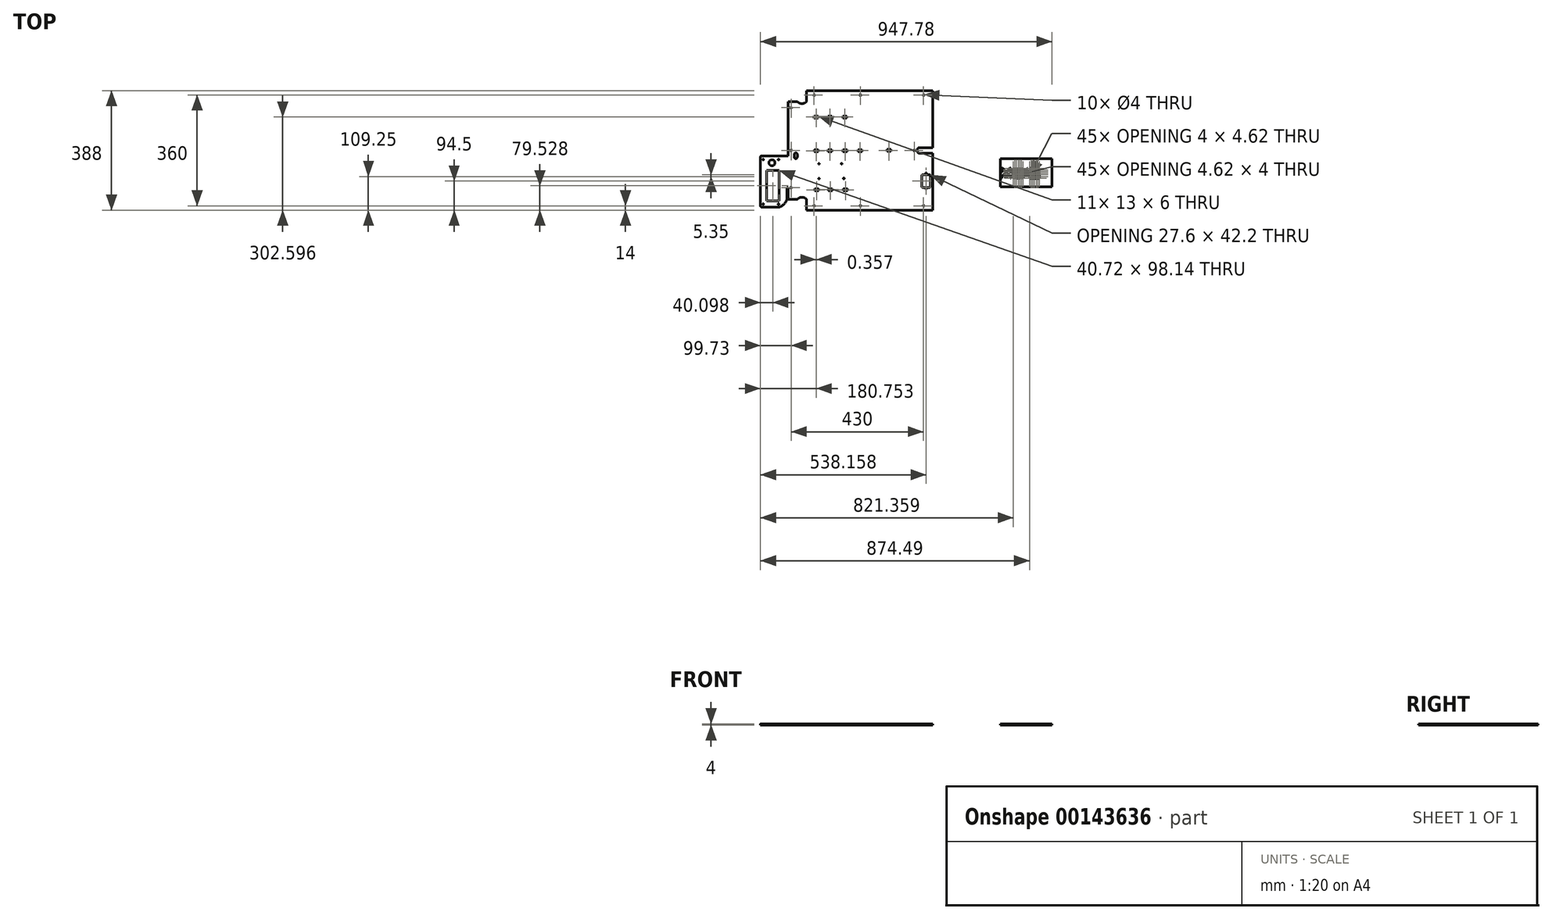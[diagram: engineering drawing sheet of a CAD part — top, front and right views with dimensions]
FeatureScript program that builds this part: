
annotation { "Feature Type Name" : "Feature", "Feature Type Description" : "" }
export const myFeature = defineFeature(function(context is Context, id is Id, definition is map)
    precondition{}
    {
        {
            var Q0;
            Q0=qCreatedBy(makeId("Top.planeOp"),FACE);
            var sketch = newSketch(context, id + "F0", { "sketchPlane" : qUnion([Q0])});
            skLineSegment(sketch, "E0.right", {"start": v(235, 190) * mm, "end": v(235, 20) * mm});
            skPoint(sketch, "E0.middle", {"position": v(0, 0) * mm});
            skLineSegment(sketch, "E1.MirrorCS", {"start": v(215, 190) * mm, "end": v(215, 170) * mm, "construction": true});
            skLineSegment(sketch, "E2.MirrorCS", {"start": v(235, 170) * mm, "end": v(215, 170) * mm, "construction": true});
            skLineSegment(sketch, "E3", {"start": v(215, 170) * mm, "end": v(215, 0) * mm, "construction": true});
            skLineSegment(sketch, "E4", {"start": v(173, 0) * mm, "end": v(215, 0) * mm, "construction": true});
            skLineSegment(sketch, "E5.top", {"start": v(235, 194) * mm, "end": v(-175, 194) * mm});
            skLineSegment(sketch, "E5.left", {"start": v(235, 190) * mm, "end": v(235, 194) * mm});
            skLineSegment(sketch, "E6", {"start": v(-235, 159) * mm, "end": v(-235, 0) * mm});
            skLineSegment(sketch, "E7", {"start": v(-175, 194) * mm, "end": v(-175, 159) * mm});
            skLineSegment(sketch, "E8", {"start": v(-175, 159) * mm, "end": v(-235, 159) * mm});
            skCircle(sketch, "E9", {"center": v(175, 0) * mm, "radius": 2 * mm});
            skCircle(sketch, "E10", {"center": v(-225, 0) * mm, "radius": 2 * mm});
            skLineSegment(sketch, "E11.bottom", {"start": v(199.63, -74) * mm, "end": v(227.23, -74) * mm, "construction": true});
            skLineSegment(sketch, "E11.top", {"start": v(199.63, -125) * mm, "end": v(227.23, -125) * mm, "construction": true});
            skLineSegment(sketch, "E11.left", {"start": v(199.63, -81.4) * mm, "end": v(199.63, -117.6) * mm});
            skLineSegment(sketch, "E11.right", {"start": v(227.23, -81.4) * mm, "end": v(227.23, -117.6) * mm});
            skPoint(sketch, "E11.middle", {"position": v(213.43, -99.5) * mm});
            skCircle(sketch, "E12", {"center": v(213.43, -125) * mm, "radius": 1.5 * mm});
            skCircle(sketch, "E13", {"center": v(213.43, -74) * mm, "radius": 1.5 * mm});
            skLineSegment(sketch, "E14", {"start": v(202.63, -120.6) * mm, "end": v(224.23, -120.6) * mm});
            skLineSegment(sketch, "E15", {"start": v(213.43, -99.5) * mm, "end": v(226.59, -99.5) * mm, "construction": true});
            skLineSegment(sketch, "E16.MirrorCS", {"start": v(202.63, -78.4) * mm, "end": v(224.23, -78.4) * mm});
            skArc(sketch, "E17.filletArc", {"start": v(199.63, -117.6) * mm, "mid": v(200.5, -119.72) * mm, "end": v(202.63, -120.6) * mm});
            skPoint(sketch, "E18.visualSharp", {"position": v(199.63, -78.4) * mm});
            skArc(sketch, "E18.filletArc", {"start": v(202.63, -78.4) * mm, "mid": v(200.5, -79.28) * mm, "end": v(199.63, -81.4) * mm});
            skPoint(sketch, "E19.visualSharp", {"position": v(227.23, -78.4) * mm});
            skArc(sketch, "E19.filletArc", {"start": v(227.23, -81.4) * mm, "mid": v(226.35, -79.28) * mm, "end": v(224.23, -78.4) * mm});
            skArc(sketch, "E20.filletArc", {"start": v(224.23, -120.6) * mm, "mid": v(226.35, -119.72) * mm, "end": v(227.23, -117.6) * mm});
            skLineSegment(sketch, "E21.trimOffspring", {"start": v(-175, 190) * mm, "end": v(235, 190) * mm, "construction": true});
            skPoint(sketch, "E22.orphan", {"position": v(122.36, 0) * mm});
            skCircle(sketch, "E23.MirrorC", {"center": v(-225, 139) * mm, "radius": 2 * mm});
            skLineSegment(sketch, "E24", {"start": v(-235, 0) * mm, "end": v(-210, 0) * mm});
            skPoint(sketch, "E24.endSnap0", {"position": v(-235, -50) * mm});
            skPoint(sketch, "E25", {"position": v(-175, 180) * mm});
            skLineSegment(sketch, "E26", {"start": v(-175, 180) * mm, "end": v(0, 180) * mm, "construction": true});
            skLineSegment(sketch, "E27", {"start": v(0, 180) * mm, "end": v(175, 180) * mm, "construction": true});
            skLineSegment(sketch, "E28", {"start": v(175, 180) * mm, "end": v(235, 180) * mm, "construction": true});
            skCircle(sketch, "E29", {"center": v(-150.66, 180) * mm, "radius": 2 * mm});
            skCircle(sketch, "E30", {"center": v(205, 180) * mm, "radius": 2 * mm});
            skCircle(sketch, "E31", {"center": v(0, 180) * mm, "radius": 2 * mm});
            skLineSegment(sketch, "E32.MirrorCS", {"start": v(-175, -159) * mm, "end": v(-235, -159) * mm});
            skLineSegment(sketch, "E33.MirrorCS", {"start": v(235, -194) * mm, "end": v(-175, -194) * mm});
            skLineSegment(sketch, "E34.MirrorCS", {"start": v(235, -190) * mm, "end": v(235, -20) * mm});
            skLineSegment(sketch, "E35.MirrorCS", {"start": v(235, -190) * mm, "end": v(235, -194) * mm});
            skLineSegment(sketch, "E36.MirrorCS", {"start": v(-175, -194) * mm, "end": v(-175, -159) * mm});
            skCircle(sketch, "E37.MirrorC", {"center": v(-225, -121) * mm, "radius": 2 * mm});
            skCircle(sketch, "E38.MirrorC", {"center": v(-150.66, -180) * mm, "radius": 2 * mm});
            skCircle(sketch, "E39.MirrorC", {"center": v(0, -180) * mm, "radius": 2 * mm});
            skCircle(sketch, "E40.MirrorC", {"center": v(205, -180) * mm, "radius": 2 * mm});
            skLineSegment(sketch, "E41", {"start": v(160.22, 194) * mm, "end": v(160.22, -194) * mm, "construction": true});
            skPoint(sketch, "E42", {"position": v(160.22, 155.68) * mm});
            skLineSegment(sketch, "E43", {"start": v(160.22, 155.68) * mm, "end": v(160.22, 194) * mm});
            skLineSegment(sketch, "E44", {"start": v(-175, 155.68) * mm, "end": v(-175, 159) * mm});
            skLineSegment(sketch, "E45.MirrorCS", {"start": v(-175, -155.68) * mm, "end": v(-175, -159) * mm});
            skLineSegment(sketch, "E46", {"start": v(160.22, -155.68) * mm, "end": v(160.22, -194) * mm});
            skCircle(sketch, "E47", {"center": v(-315.8, -174.64) * mm, "radius": 1.5 * mm});
            skCircle(sketch, "E48", {"center": v(-265.85, -174.82) * mm, "radius": 1.5 * mm});
            skCircle(sketch, "E49", {"center": v(-265.85, -29.64) * mm, "radius": 1.5 * mm});
            skCircle(sketch, "E50", {"center": v(-315.85, -29.64) * mm, "radius": 1.5 * mm});
            skLineSegment(sketch, "E51", {"start": v(-235, -184.73) * mm, "end": v(-319.73, -184.73) * mm});
            skLineSegment(sketch, "E52", {"start": v(-324.73, -179.73) * mm, "end": v(-324.73, -21.83) * mm});
            skPoint(sketch, "E53.visualSharp", {"position": v(-324.73, -184.73) * mm});
            skArc(sketch, "E53.filletArc", {"start": v(-324.73, -179.73) * mm, "mid": v(-323.27, -183.27) * mm, "end": v(-319.73, -184.73) * mm});
            skPoint(sketch, "E54.visualSharp", {"position": v(-324.73, -19.02) * mm});
            skArc(sketch, "E54.filletArc", {"start": v(-322.37, -17.58) * mm, "mid": v(-324.1, -19.4) * mm, "end": v(-324.73, -21.83) * mm});
            skCircle(sketch, "E55", {"center": v(-53.85, -91.06) * mm, "radius": 1.5 * mm});
            skCircle(sketch, "E56", {"center": v(-61.23, -43.24) * mm, "radius": 1.5 * mm});
            skCircle(sketch, "E57", {"center": v(-134.56, -43.33) * mm, "radius": 1.5 * mm});
            skCircle(sketch, "E58", {"center": v(-134.56, -91.36) * mm, "radius": 1.5 * mm});
            skCircle(sketch, "E59.MirrorC", {"center": v(-287.35, -40.12) * mm, "radius": 10 * mm});
            skLineSegment(sketch, "E60.bottom", {"start": v(-305, -163.54) * mm, "end": v(-305, -65.4) * mm});
            skLineSegment(sketch, "E60.top", {"start": v(-264.27, -163.54) * mm, "end": v(-264.27, -65.4) * mm});
            skLineSegment(sketch, "E60.left", {"start": v(-305, -163.54) * mm, "end": v(-264.27, -163.54) * mm});
            skLineSegment(sketch, "E60.right", {"start": v(-305, -65.4) * mm, "end": v(-264.27, -65.4) * mm});
            skLineSegment(sketch, "E61", {"start": v(-322.37, -17.58) * mm, "end": v(-235, -17.58) * mm});
            skLineSegment(sketch, "E62", {"start": v(-235, -141.11) * mm, "end": v(-235, -141) * mm});
            skLineSegment(sketch, "E63", {"start": v(-235, -17.58) * mm, "end": v(-235, 18) * mm});
            skLineSegment(sketch, "E64", {"start": v(-235, -184.73) * mm, "end": v(-235, -119.54) * mm});
            skLineSegment(sketch, "E65", {"start": v(388.05, 194) * mm, "end": v(623.05, 194) * mm});
            skLineSegment(sketch, "E66", {"start": v(623.05, 194) * mm, "end": v(623.05, -194) * mm});
            skPoint(sketch, "E67", {"position": v(488.05, 194) * mm});
            skArc(sketch, "E68", {"start": v(488.05, 194) * mm, "mid": v(391.69, 0) * mm, "end": v(488.05, -194) * mm});
            skLineSegment(sketch, "E69", {"start": v(488.05, -194) * mm, "end": v(623.05, -194) * mm});
            skLineSegment(sketch, "E70.bottom", {"start": v(532.63, -94) * mm, "end": v(492.63, -94) * mm, "construction": true});
            skLineSegment(sketch, "E70.top", {"start": v(532.63, -54) * mm, "end": v(492.63, -54) * mm, "construction": true});
            skLineSegment(sketch, "E70.left", {"start": v(532.63, -94) * mm, "end": v(532.63, -54) * mm, "construction": true});
            skLineSegment(sketch, "E70.right", {"start": v(492.63, -94) * mm, "end": v(492.63, -54) * mm, "construction": true});
            skPoint(sketch, "E70.middle", {"position": v(512.63, -74) * mm});
            skLineSegment(sketch, "E71.bottom", {"start": v(585.76, -94) * mm, "end": v(545.76, -94) * mm, "construction": true});
            skLineSegment(sketch, "E71.top", {"start": v(585.76, -54) * mm, "end": v(545.76, -54) * mm, "construction": true});
            skLineSegment(sketch, "E71.left", {"start": v(585.76, -94) * mm, "end": v(585.76, -54) * mm, "construction": true});
            skLineSegment(sketch, "E71.right", {"start": v(545.76, -94) * mm, "end": v(545.76, -54) * mm, "construction": true});
            skPoint(sketch, "E71.middle", {"position": v(565.76, -74) * mm});
            skLineSegment(sketch, "E72", {"start": v(532.63, -54) * mm, "end": v(545.76, -54) * mm, "construction": true});
            skLineSegment(sketch, "E73.bottom", {"start": v(528.63, -58) * mm, "end": v(496.63, -58) * mm, "construction": true});
            skLineSegment(sketch, "E73.top", {"start": v(528.63, -90) * mm, "end": v(496.63, -90) * mm, "construction": true});
            skLineSegment(sketch, "E73.left", {"start": v(528.63, -58) * mm, "end": v(528.63, -90) * mm, "construction": true});
            skLineSegment(sketch, "E73.right", {"start": v(496.63, -58) * mm, "end": v(496.63, -90) * mm, "construction": true});
            skLineSegment(sketch, "E74.bottom", {"start": v(581.76, -58) * mm, "end": v(549.76, -58) * mm, "construction": true});
            skLineSegment(sketch, "E74.top", {"start": v(581.76, -90) * mm, "end": v(549.76, -90) * mm, "construction": true});
            skLineSegment(sketch, "E74.left", {"start": v(581.76, -58) * mm, "end": v(581.76, -90) * mm, "construction": true});
            skLineSegment(sketch, "E74.right", {"start": v(549.76, -58) * mm, "end": v(549.76, -90) * mm, "construction": true});
            skLineSegment(sketch, "E75.0.1.0", {"start": v(495.47, -61.35) * mm, "end": v(497.78, -61.35) * mm});
            skPoint(sketch, "E75.0.1.1", {"position": v(496.63, -61.35) * mm});
            skLineSegment(sketch, "E75.0.1.2", {"start": v(497.78, -61.35) * mm, "end": v(498.94, -63.35) * mm});
            skLineSegment(sketch, "E75.0.1.3", {"start": v(495.47, -65.35) * mm, "end": v(494.32, -63.35) * mm});
            skLineSegment(sketch, "E75.0.1.4", {"start": v(497.78, -65.35) * mm, "end": v(495.47, -65.35) * mm});
            skCircle(sketch, "E75.0.1.5", {"center": v(496.63, -63.35) * mm, "radius": 2 * mm, "construction": true});
            skLineSegment(sketch, "E75.0.1.6", {"start": v(494.32, -63.35) * mm, "end": v(495.47, -61.35) * mm});
            skLineSegment(sketch, "E75.0.1.7", {"start": v(498.94, -63.35) * mm, "end": v(497.78, -65.35) * mm});
            skLineSegment(sketch, "E75.0.2.0", {"start": v(495.47, -66.7) * mm, "end": v(497.78, -66.7) * mm});
            skPoint(sketch, "E75.0.2.1", {"position": v(496.63, -66.7) * mm});
            skLineSegment(sketch, "E75.0.2.2", {"start": v(497.78, -66.7) * mm, "end": v(498.94, -68.7) * mm});
            skLineSegment(sketch, "E75.0.2.3", {"start": v(495.47, -70.7) * mm, "end": v(494.32, -68.7) * mm});
            skLineSegment(sketch, "E75.0.2.4", {"start": v(497.78, -70.7) * mm, "end": v(495.47, -70.7) * mm});
            skCircle(sketch, "E75.0.2.5", {"center": v(496.63, -68.7) * mm, "radius": 2 * mm, "construction": true});
            skLineSegment(sketch, "E75.0.2.6", {"start": v(494.32, -68.7) * mm, "end": v(495.47, -66.7) * mm});
            skLineSegment(sketch, "E75.0.2.7", {"start": v(498.94, -68.7) * mm, "end": v(497.78, -70.7) * mm});
            skLineSegment(sketch, "E75.0.3.0", {"start": v(495.47, -72.05) * mm, "end": v(497.78, -72.05) * mm});
            skPoint(sketch, "E75.0.3.1", {"position": v(496.63, -72.05) * mm});
            skLineSegment(sketch, "E75.0.3.2", {"start": v(497.78, -72.05) * mm, "end": v(498.94, -74.05) * mm});
            skLineSegment(sketch, "E75.0.3.3", {"start": v(495.47, -76.05) * mm, "end": v(494.32, -74.05) * mm});
            skLineSegment(sketch, "E75.0.3.4", {"start": v(497.78, -76.05) * mm, "end": v(495.47, -76.05) * mm});
            skCircle(sketch, "E75.0.3.5", {"center": v(496.63, -74.05) * mm, "radius": 2 * mm, "construction": true});
            skLineSegment(sketch, "E75.0.3.6", {"start": v(494.32, -74.05) * mm, "end": v(495.47, -72.05) * mm});
            skLineSegment(sketch, "E75.0.3.7", {"start": v(498.94, -74.05) * mm, "end": v(497.78, -76.05) * mm});
            skLineSegment(sketch, "E75.0.4.0", {"start": v(495.47, -77.4) * mm, "end": v(497.78, -77.4) * mm});
            skPoint(sketch, "E75.0.4.1", {"position": v(496.63, -77.4) * mm});
            skLineSegment(sketch, "E75.0.4.2", {"start": v(497.78, -77.4) * mm, "end": v(498.94, -79.4) * mm});
            skLineSegment(sketch, "E75.0.4.3", {"start": v(495.47, -81.4) * mm, "end": v(494.32, -79.4) * mm});
            skLineSegment(sketch, "E75.0.4.4", {"start": v(497.78, -81.4) * mm, "end": v(495.47, -81.4) * mm});
            skCircle(sketch, "E75.0.4.5", {"center": v(496.63, -79.4) * mm, "radius": 2 * mm, "construction": true});
            skLineSegment(sketch, "E75.0.4.6", {"start": v(494.32, -79.4) * mm, "end": v(495.47, -77.4) * mm});
            skLineSegment(sketch, "E75.0.4.7", {"start": v(498.94, -79.4) * mm, "end": v(497.78, -81.4) * mm});
            skLineSegment(sketch, "E75.0.5.0", {"start": v(495.47, -82.75) * mm, "end": v(497.78, -82.75) * mm});
            skPoint(sketch, "E75.0.5.1", {"position": v(496.63, -82.75) * mm});
            skLineSegment(sketch, "E75.0.5.2", {"start": v(497.78, -82.75) * mm, "end": v(498.94, -84.75) * mm});
            skLineSegment(sketch, "E75.0.5.3", {"start": v(495.47, -86.75) * mm, "end": v(494.32, -84.75) * mm});
            skLineSegment(sketch, "E75.0.5.4", {"start": v(497.78, -86.75) * mm, "end": v(495.47, -86.75) * mm});
            skCircle(sketch, "E75.0.5.5", {"center": v(496.63, -84.75) * mm, "radius": 2 * mm, "construction": true});
            skLineSegment(sketch, "E75.0.5.6", {"start": v(494.32, -84.75) * mm, "end": v(495.47, -82.75) * mm});
            skLineSegment(sketch, "E75.0.5.7", {"start": v(498.94, -84.75) * mm, "end": v(497.78, -86.75) * mm});
            skLineSegment(sketch, "E75.1.0.0", {"start": v(500.82, -56) * mm, "end": v(503.13, -56) * mm});
            skPoint(sketch, "E75.1.0.1", {"position": v(501.98, -56) * mm});
            skLineSegment(sketch, "E75.1.0.2", {"start": v(503.13, -56) * mm, "end": v(504.29, -58) * mm});
            skLineSegment(sketch, "E75.1.0.3", {"start": v(500.82, -60) * mm, "end": v(499.67, -58) * mm});
            skLineSegment(sketch, "E75.1.0.4", {"start": v(503.13, -60) * mm, "end": v(500.82, -60) * mm});
            skCircle(sketch, "E75.1.0.5", {"center": v(501.98, -58) * mm, "radius": 2 * mm, "construction": true});
            skLineSegment(sketch, "E75.1.0.6", {"start": v(499.67, -58) * mm, "end": v(500.82, -56) * mm});
            skLineSegment(sketch, "E75.1.0.7", {"start": v(504.29, -58) * mm, "end": v(503.13, -60) * mm});
            skLineSegment(sketch, "E75.1.1.0", {"start": v(500.82, -61.35) * mm, "end": v(503.13, -61.35) * mm});
            skPoint(sketch, "E75.1.1.1", {"position": v(501.98, -61.35) * mm});
            skLineSegment(sketch, "E75.1.1.2", {"start": v(503.13, -61.35) * mm, "end": v(504.29, -63.35) * mm});
            skLineSegment(sketch, "E75.1.1.3", {"start": v(500.82, -65.35) * mm, "end": v(499.67, -63.35) * mm});
            skLineSegment(sketch, "E75.1.1.4", {"start": v(503.13, -65.35) * mm, "end": v(500.82, -65.35) * mm});
            skCircle(sketch, "E75.1.1.5", {"center": v(501.98, -63.35) * mm, "radius": 2 * mm, "construction": true});
            skLineSegment(sketch, "E75.1.1.6", {"start": v(499.67, -63.35) * mm, "end": v(500.82, -61.35) * mm});
            skLineSegment(sketch, "E75.1.1.7", {"start": v(504.29, -63.35) * mm, "end": v(503.13, -65.35) * mm});
            skLineSegment(sketch, "E75.1.2.0", {"start": v(500.82, -66.7) * mm, "end": v(503.13, -66.7) * mm});
            skPoint(sketch, "E75.1.2.1", {"position": v(501.98, -66.7) * mm});
            skLineSegment(sketch, "E75.1.2.2", {"start": v(503.13, -66.7) * mm, "end": v(504.29, -68.7) * mm});
            skLineSegment(sketch, "E75.1.2.3", {"start": v(500.82, -70.7) * mm, "end": v(499.67, -68.7) * mm});
            skLineSegment(sketch, "E75.1.2.4", {"start": v(503.13, -70.7) * mm, "end": v(500.82, -70.7) * mm});
            skCircle(sketch, "E75.1.2.5", {"center": v(501.98, -68.7) * mm, "radius": 2 * mm, "construction": true});
            skLineSegment(sketch, "E75.1.2.6", {"start": v(499.67, -68.7) * mm, "end": v(500.82, -66.7) * mm});
            skLineSegment(sketch, "E75.1.2.7", {"start": v(504.29, -68.7) * mm, "end": v(503.13, -70.7) * mm});
            skLineSegment(sketch, "E75.1.3.0", {"start": v(500.82, -72.05) * mm, "end": v(503.13, -72.05) * mm});
            skPoint(sketch, "E75.1.3.1", {"position": v(501.98, -72.05) * mm});
            skLineSegment(sketch, "E75.1.3.2", {"start": v(503.13, -72.05) * mm, "end": v(504.29, -74.05) * mm});
            skLineSegment(sketch, "E75.1.3.3", {"start": v(500.82, -76.05) * mm, "end": v(499.67, -74.05) * mm});
            skLineSegment(sketch, "E75.1.3.4", {"start": v(503.13, -76.05) * mm, "end": v(500.82, -76.05) * mm});
            skCircle(sketch, "E75.1.3.5", {"center": v(501.98, -74.05) * mm, "radius": 2 * mm, "construction": true});
            skLineSegment(sketch, "E75.1.3.6", {"start": v(499.67, -74.05) * mm, "end": v(500.82, -72.05) * mm});
            skLineSegment(sketch, "E75.1.3.7", {"start": v(504.29, -74.05) * mm, "end": v(503.13, -76.05) * mm});
            skLineSegment(sketch, "E75.1.4.0", {"start": v(500.82, -77.4) * mm, "end": v(503.13, -77.4) * mm});
            skPoint(sketch, "E75.1.4.1", {"position": v(501.98, -77.4) * mm});
            skLineSegment(sketch, "E75.1.4.2", {"start": v(503.13, -77.4) * mm, "end": v(504.29, -79.4) * mm});
            skLineSegment(sketch, "E75.1.4.3", {"start": v(500.82, -81.4) * mm, "end": v(499.67, -79.4) * mm});
            skLineSegment(sketch, "E75.1.4.4", {"start": v(503.13, -81.4) * mm, "end": v(500.82, -81.4) * mm});
            skCircle(sketch, "E75.1.4.5", {"center": v(501.98, -79.4) * mm, "radius": 2 * mm, "construction": true});
            skLineSegment(sketch, "E75.1.4.6", {"start": v(499.67, -79.4) * mm, "end": v(500.82, -77.4) * mm});
            skLineSegment(sketch, "E75.1.4.7", {"start": v(504.29, -79.4) * mm, "end": v(503.13, -81.4) * mm});
            skLineSegment(sketch, "E75.1.5.0", {"start": v(500.82, -82.75) * mm, "end": v(503.13, -82.75) * mm});
            skPoint(sketch, "E75.1.5.1", {"position": v(501.98, -82.75) * mm});
            skLineSegment(sketch, "E75.1.5.2", {"start": v(503.13, -82.75) * mm, "end": v(504.29, -84.75) * mm});
            skLineSegment(sketch, "E75.1.5.3", {"start": v(500.82, -86.75) * mm, "end": v(499.67, -84.75) * mm});
            skLineSegment(sketch, "E75.1.5.4", {"start": v(503.13, -86.75) * mm, "end": v(500.82, -86.75) * mm});
            skCircle(sketch, "E75.1.5.5", {"center": v(501.98, -84.75) * mm, "radius": 2 * mm, "construction": true});
            skLineSegment(sketch, "E75.1.5.6", {"start": v(499.67, -84.75) * mm, "end": v(500.82, -82.75) * mm});
            skLineSegment(sketch, "E75.1.5.7", {"start": v(504.29, -84.75) * mm, "end": v(503.13, -86.75) * mm});
            skLineSegment(sketch, "E75.1.6.0", {"start": v(500.82, -88.1) * mm, "end": v(503.13, -88.1) * mm});
            skPoint(sketch, "E75.1.6.1", {"position": v(501.98, -88.1) * mm});
            skLineSegment(sketch, "E75.1.6.2", {"start": v(503.13, -88.1) * mm, "end": v(504.29, -90.1) * mm});
            skLineSegment(sketch, "E75.1.6.3", {"start": v(500.82, -92.1) * mm, "end": v(499.67, -90.1) * mm});
            skLineSegment(sketch, "E75.1.6.4", {"start": v(503.13, -92.1) * mm, "end": v(500.82, -92.1) * mm});
            skCircle(sketch, "E75.1.6.5", {"center": v(501.98, -90.1) * mm, "radius": 2 * mm, "construction": true});
            skLineSegment(sketch, "E75.1.6.6", {"start": v(499.67, -90.1) * mm, "end": v(500.82, -88.1) * mm});
            skLineSegment(sketch, "E75.1.6.7", {"start": v(504.29, -90.1) * mm, "end": v(503.13, -92.1) * mm});
            skLineSegment(sketch, "E75.2.0.0", {"start": v(506.17, -56) * mm, "end": v(508.48, -56) * mm});
            skPoint(sketch, "E75.2.0.1", {"position": v(507.33, -56) * mm});
            skLineSegment(sketch, "E75.2.0.2", {"start": v(508.48, -56) * mm, "end": v(509.64, -58) * mm});
            skLineSegment(sketch, "E75.2.0.3", {"start": v(506.17, -60) * mm, "end": v(505.02, -58) * mm});
            skLineSegment(sketch, "E75.2.0.4", {"start": v(508.48, -60) * mm, "end": v(506.17, -60) * mm});
            skCircle(sketch, "E75.2.0.5", {"center": v(507.33, -58) * mm, "radius": 2 * mm, "construction": true});
            skLineSegment(sketch, "E75.2.0.6", {"start": v(505.02, -58) * mm, "end": v(506.17, -56) * mm});
            skLineSegment(sketch, "E75.2.0.7", {"start": v(509.64, -58) * mm, "end": v(508.48, -60) * mm});
            skLineSegment(sketch, "E75.2.1.0", {"start": v(506.17, -61.35) * mm, "end": v(508.48, -61.35) * mm});
            skPoint(sketch, "E75.2.1.1", {"position": v(507.33, -61.35) * mm});
            skLineSegment(sketch, "E75.2.1.2", {"start": v(508.48, -61.35) * mm, "end": v(509.64, -63.35) * mm});
            skLineSegment(sketch, "E75.2.1.3", {"start": v(506.17, -65.35) * mm, "end": v(505.02, -63.35) * mm});
            skLineSegment(sketch, "E75.2.1.4", {"start": v(508.48, -65.35) * mm, "end": v(506.17, -65.35) * mm});
            skCircle(sketch, "E75.2.1.5", {"center": v(507.33, -63.35) * mm, "radius": 2 * mm, "construction": true});
            skLineSegment(sketch, "E75.2.1.6", {"start": v(505.02, -63.35) * mm, "end": v(506.17, -61.35) * mm});
            skLineSegment(sketch, "E75.2.1.7", {"start": v(509.64, -63.35) * mm, "end": v(508.48, -65.35) * mm});
            skLineSegment(sketch, "E75.2.2.0", {"start": v(506.17, -66.7) * mm, "end": v(508.48, -66.7) * mm});
            skPoint(sketch, "E75.2.2.1", {"position": v(507.33, -66.7) * mm});
            skLineSegment(sketch, "E75.2.2.2", {"start": v(508.48, -66.7) * mm, "end": v(509.64, -68.7) * mm});
            skLineSegment(sketch, "E75.2.2.3", {"start": v(506.17, -70.7) * mm, "end": v(505.02, -68.7) * mm});
            skLineSegment(sketch, "E75.2.2.4", {"start": v(508.48, -70.7) * mm, "end": v(506.17, -70.7) * mm});
            skCircle(sketch, "E75.2.2.5", {"center": v(507.33, -68.7) * mm, "radius": 2 * mm, "construction": true});
            skLineSegment(sketch, "E75.2.2.6", {"start": v(505.02, -68.7) * mm, "end": v(506.17, -66.7) * mm});
            skLineSegment(sketch, "E75.2.2.7", {"start": v(509.64, -68.7) * mm, "end": v(508.48, -70.7) * mm});
            skLineSegment(sketch, "E75.2.3.0", {"start": v(506.17, -72.05) * mm, "end": v(508.48, -72.05) * mm});
            skPoint(sketch, "E75.2.3.1", {"position": v(507.33, -72.05) * mm});
            skLineSegment(sketch, "E75.2.3.2", {"start": v(508.48, -72.05) * mm, "end": v(509.64, -74.05) * mm});
            skLineSegment(sketch, "E75.2.3.3", {"start": v(506.17, -76.05) * mm, "end": v(505.02, -74.05) * mm});
            skLineSegment(sketch, "E75.2.3.4", {"start": v(508.48, -76.05) * mm, "end": v(506.17, -76.05) * mm});
            skCircle(sketch, "E75.2.3.5", {"center": v(507.33, -74.05) * mm, "radius": 2 * mm, "construction": true});
            skLineSegment(sketch, "E75.2.3.6", {"start": v(505.02, -74.05) * mm, "end": v(506.17, -72.05) * mm});
            skLineSegment(sketch, "E75.2.3.7", {"start": v(509.64, -74.05) * mm, "end": v(508.48, -76.05) * mm});
            skLineSegment(sketch, "E75.2.4.0", {"start": v(506.17, -77.4) * mm, "end": v(508.48, -77.4) * mm});
            skPoint(sketch, "E75.2.4.1", {"position": v(507.33, -77.4) * mm});
            skLineSegment(sketch, "E75.2.4.2", {"start": v(508.48, -77.4) * mm, "end": v(509.64, -79.4) * mm});
            skLineSegment(sketch, "E75.2.4.3", {"start": v(506.17, -81.4) * mm, "end": v(505.02, -79.4) * mm});
            skLineSegment(sketch, "E75.2.4.4", {"start": v(508.48, -81.4) * mm, "end": v(506.17, -81.4) * mm});
            skCircle(sketch, "E75.2.4.5", {"center": v(507.33, -79.4) * mm, "radius": 2 * mm, "construction": true});
            skLineSegment(sketch, "E75.2.4.6", {"start": v(505.02, -79.4) * mm, "end": v(506.17, -77.4) * mm});
            skLineSegment(sketch, "E75.2.4.7", {"start": v(509.64, -79.4) * mm, "end": v(508.48, -81.4) * mm});
            skLineSegment(sketch, "E75.2.5.0", {"start": v(506.17, -82.75) * mm, "end": v(508.48, -82.75) * mm});
            skPoint(sketch, "E75.2.5.1", {"position": v(507.33, -82.75) * mm});
            skLineSegment(sketch, "E75.2.5.2", {"start": v(508.48, -82.75) * mm, "end": v(509.64, -84.75) * mm});
            skLineSegment(sketch, "E75.2.5.3", {"start": v(506.17, -86.75) * mm, "end": v(505.02, -84.75) * mm});
            skLineSegment(sketch, "E75.2.5.4", {"start": v(508.48, -86.75) * mm, "end": v(506.17, -86.75) * mm});
            skCircle(sketch, "E75.2.5.5", {"center": v(507.33, -84.75) * mm, "radius": 2 * mm, "construction": true});
            skLineSegment(sketch, "E75.2.5.6", {"start": v(505.02, -84.75) * mm, "end": v(506.17, -82.75) * mm});
            skLineSegment(sketch, "E75.2.5.7", {"start": v(509.64, -84.75) * mm, "end": v(508.48, -86.75) * mm});
            skLineSegment(sketch, "E75.2.6.0", {"start": v(506.17, -88.1) * mm, "end": v(508.48, -88.1) * mm});
            skPoint(sketch, "E75.2.6.1", {"position": v(507.33, -88.1) * mm});
            skLineSegment(sketch, "E75.2.6.2", {"start": v(508.48, -88.1) * mm, "end": v(509.64, -90.1) * mm});
            skLineSegment(sketch, "E75.2.6.3", {"start": v(506.17, -92.1) * mm, "end": v(505.02, -90.1) * mm});
            skLineSegment(sketch, "E75.2.6.4", {"start": v(508.48, -92.1) * mm, "end": v(506.17, -92.1) * mm});
            skCircle(sketch, "E75.2.6.5", {"center": v(507.33, -90.1) * mm, "radius": 2 * mm, "construction": true});
            skLineSegment(sketch, "E75.2.6.6", {"start": v(505.02, -90.1) * mm, "end": v(506.17, -88.1) * mm});
            skLineSegment(sketch, "E75.2.6.7", {"start": v(509.64, -90.1) * mm, "end": v(508.48, -92.1) * mm});
            skLineSegment(sketch, "E75.3.0.0", {"start": v(511.52, -56) * mm, "end": v(513.83, -56) * mm});
            skPoint(sketch, "E75.3.0.1", {"position": v(512.68, -56) * mm});
            skLineSegment(sketch, "E75.3.0.2", {"start": v(513.83, -56) * mm, "end": v(514.99, -58) * mm});
            skLineSegment(sketch, "E75.3.0.3", {"start": v(511.52, -60) * mm, "end": v(510.37, -58) * mm});
            skLineSegment(sketch, "E75.3.0.4", {"start": v(513.83, -60) * mm, "end": v(511.52, -60) * mm});
            skCircle(sketch, "E75.3.0.5", {"center": v(512.68, -58) * mm, "radius": 2 * mm, "construction": true});
            skLineSegment(sketch, "E75.3.0.6", {"start": v(510.37, -58) * mm, "end": v(511.52, -56) * mm});
            skLineSegment(sketch, "E75.3.0.7", {"start": v(514.99, -58) * mm, "end": v(513.83, -60) * mm});
            skLineSegment(sketch, "E75.3.1.0", {"start": v(511.52, -61.35) * mm, "end": v(513.83, -61.35) * mm});
            skPoint(sketch, "E75.3.1.1", {"position": v(512.68, -61.35) * mm});
            skLineSegment(sketch, "E75.3.1.2", {"start": v(513.83, -61.35) * mm, "end": v(514.99, -63.35) * mm});
            skLineSegment(sketch, "E75.3.1.3", {"start": v(511.52, -65.35) * mm, "end": v(510.37, -63.35) * mm});
            skLineSegment(sketch, "E75.3.1.4", {"start": v(513.83, -65.35) * mm, "end": v(511.52, -65.35) * mm});
            skCircle(sketch, "E75.3.1.5", {"center": v(512.68, -63.35) * mm, "radius": 2 * mm, "construction": true});
            skLineSegment(sketch, "E75.3.1.6", {"start": v(510.37, -63.35) * mm, "end": v(511.52, -61.35) * mm});
            skLineSegment(sketch, "E75.3.1.7", {"start": v(514.99, -63.35) * mm, "end": v(513.83, -65.35) * mm});
            skLineSegment(sketch, "E75.3.2.0", {"start": v(511.52, -66.7) * mm, "end": v(513.83, -66.7) * mm});
            skPoint(sketch, "E75.3.2.1", {"position": v(512.68, -66.7) * mm});
            skLineSegment(sketch, "E75.3.2.2", {"start": v(513.83, -66.7) * mm, "end": v(514.99, -68.7) * mm});
            skLineSegment(sketch, "E75.3.2.3", {"start": v(511.52, -70.7) * mm, "end": v(510.37, -68.7) * mm});
            skLineSegment(sketch, "E75.3.2.4", {"start": v(513.83, -70.7) * mm, "end": v(511.52, -70.7) * mm});
            skCircle(sketch, "E75.3.2.5", {"center": v(512.68, -68.7) * mm, "radius": 2 * mm, "construction": true});
            skLineSegment(sketch, "E75.3.2.6", {"start": v(510.37, -68.7) * mm, "end": v(511.52, -66.7) * mm});
            skLineSegment(sketch, "E75.3.2.7", {"start": v(514.99, -68.7) * mm, "end": v(513.83, -70.7) * mm});
            skLineSegment(sketch, "E75.3.3.0", {"start": v(511.52, -72.05) * mm, "end": v(513.83, -72.05) * mm});
            skPoint(sketch, "E75.3.3.1", {"position": v(512.68, -72.05) * mm});
            skLineSegment(sketch, "E75.3.3.2", {"start": v(513.83, -72.05) * mm, "end": v(514.99, -74.05) * mm});
            skLineSegment(sketch, "E75.3.3.3", {"start": v(511.52, -76.05) * mm, "end": v(510.37, -74.05) * mm});
            skLineSegment(sketch, "E75.3.3.4", {"start": v(513.83, -76.05) * mm, "end": v(511.52, -76.05) * mm});
            skCircle(sketch, "E75.3.3.5", {"center": v(512.68, -74.05) * mm, "radius": 2 * mm, "construction": true});
            skLineSegment(sketch, "E75.3.3.6", {"start": v(510.37, -74.05) * mm, "end": v(511.52, -72.05) * mm});
            skLineSegment(sketch, "E75.3.3.7", {"start": v(514.99, -74.05) * mm, "end": v(513.83, -76.05) * mm});
            skLineSegment(sketch, "E75.3.4.0", {"start": v(511.52, -77.4) * mm, "end": v(513.83, -77.4) * mm});
            skPoint(sketch, "E75.3.4.1", {"position": v(512.68, -77.4) * mm});
            skLineSegment(sketch, "E75.3.4.2", {"start": v(513.83, -77.4) * mm, "end": v(514.99, -79.4) * mm});
            skLineSegment(sketch, "E75.3.4.3", {"start": v(511.52, -81.4) * mm, "end": v(510.37, -79.4) * mm});
            skLineSegment(sketch, "E75.3.4.4", {"start": v(513.83, -81.4) * mm, "end": v(511.52, -81.4) * mm});
            skCircle(sketch, "E75.3.4.5", {"center": v(512.68, -79.4) * mm, "radius": 2 * mm, "construction": true});
            skLineSegment(sketch, "E75.3.4.6", {"start": v(510.37, -79.4) * mm, "end": v(511.52, -77.4) * mm});
            skLineSegment(sketch, "E75.3.4.7", {"start": v(514.99, -79.4) * mm, "end": v(513.83, -81.4) * mm});
            skLineSegment(sketch, "E75.3.5.0", {"start": v(511.52, -82.75) * mm, "end": v(513.83, -82.75) * mm});
            skPoint(sketch, "E75.3.5.1", {"position": v(512.68, -82.75) * mm});
            skLineSegment(sketch, "E75.3.5.2", {"start": v(513.83, -82.75) * mm, "end": v(514.99, -84.75) * mm});
            skLineSegment(sketch, "E75.3.5.3", {"start": v(511.52, -86.75) * mm, "end": v(510.37, -84.75) * mm});
            skLineSegment(sketch, "E75.3.5.4", {"start": v(513.83, -86.75) * mm, "end": v(511.52, -86.75) * mm});
            skCircle(sketch, "E75.3.5.5", {"center": v(512.68, -84.75) * mm, "radius": 2 * mm, "construction": true});
            skLineSegment(sketch, "E75.3.5.6", {"start": v(510.37, -84.75) * mm, "end": v(511.52, -82.75) * mm});
            skLineSegment(sketch, "E75.3.5.7", {"start": v(514.99, -84.75) * mm, "end": v(513.83, -86.75) * mm});
            skLineSegment(sketch, "E75.3.6.0", {"start": v(511.52, -88.1) * mm, "end": v(513.83, -88.1) * mm});
            skPoint(sketch, "E75.3.6.1", {"position": v(512.68, -88.1) * mm});
            skLineSegment(sketch, "E75.3.6.2", {"start": v(513.83, -88.1) * mm, "end": v(514.99, -90.1) * mm});
            skLineSegment(sketch, "E75.3.6.3", {"start": v(511.52, -92.1) * mm, "end": v(510.37, -90.1) * mm});
            skLineSegment(sketch, "E75.3.6.4", {"start": v(513.83, -92.1) * mm, "end": v(511.52, -92.1) * mm});
            skCircle(sketch, "E75.3.6.5", {"center": v(512.68, -90.1) * mm, "radius": 2 * mm, "construction": true});
            skLineSegment(sketch, "E75.3.6.6", {"start": v(510.37, -90.1) * mm, "end": v(511.52, -88.1) * mm});
            skLineSegment(sketch, "E75.3.6.7", {"start": v(514.99, -90.1) * mm, "end": v(513.83, -92.1) * mm});
            skLineSegment(sketch, "E75.4.0.0", {"start": v(516.87, -56) * mm, "end": v(519.18, -56) * mm});
            skPoint(sketch, "E75.4.0.1", {"position": v(518.03, -56) * mm});
            skLineSegment(sketch, "E75.4.0.2", {"start": v(519.18, -56) * mm, "end": v(520.34, -58) * mm});
            skLineSegment(sketch, "E75.4.0.3", {"start": v(516.87, -60) * mm, "end": v(515.72, -58) * mm});
            skLineSegment(sketch, "E75.4.0.4", {"start": v(519.18, -60) * mm, "end": v(516.87, -60) * mm});
            skCircle(sketch, "E75.4.0.5", {"center": v(518.03, -58) * mm, "radius": 2 * mm, "construction": true});
            skLineSegment(sketch, "E75.4.0.6", {"start": v(515.72, -58) * mm, "end": v(516.87, -56) * mm});
            skLineSegment(sketch, "E75.4.0.7", {"start": v(520.34, -58) * mm, "end": v(519.18, -60) * mm});
            skLineSegment(sketch, "E75.4.1.0", {"start": v(516.87, -61.35) * mm, "end": v(519.18, -61.35) * mm});
            skPoint(sketch, "E75.4.1.1", {"position": v(518.03, -61.35) * mm});
            skLineSegment(sketch, "E75.4.1.2", {"start": v(519.18, -61.35) * mm, "end": v(520.34, -63.35) * mm});
            skLineSegment(sketch, "E75.4.1.3", {"start": v(516.87, -65.35) * mm, "end": v(515.72, -63.35) * mm});
            skLineSegment(sketch, "E75.4.1.4", {"start": v(519.18, -65.35) * mm, "end": v(516.87, -65.35) * mm});
            skCircle(sketch, "E75.4.1.5", {"center": v(518.03, -63.35) * mm, "radius": 2 * mm, "construction": true});
            skLineSegment(sketch, "E75.4.1.6", {"start": v(515.72, -63.35) * mm, "end": v(516.87, -61.35) * mm});
            skLineSegment(sketch, "E75.4.1.7", {"start": v(520.34, -63.35) * mm, "end": v(519.18, -65.35) * mm});
            skLineSegment(sketch, "E75.4.2.0", {"start": v(516.87, -66.7) * mm, "end": v(519.18, -66.7) * mm});
            skPoint(sketch, "E75.4.2.1", {"position": v(518.03, -66.7) * mm});
            skLineSegment(sketch, "E75.4.2.2", {"start": v(519.18, -66.7) * mm, "end": v(520.34, -68.7) * mm});
            skLineSegment(sketch, "E75.4.2.3", {"start": v(516.87, -70.7) * mm, "end": v(515.72, -68.7) * mm});
            skLineSegment(sketch, "E75.4.2.4", {"start": v(519.18, -70.7) * mm, "end": v(516.87, -70.7) * mm});
            skCircle(sketch, "E75.4.2.5", {"center": v(518.03, -68.7) * mm, "radius": 2 * mm, "construction": true});
            skLineSegment(sketch, "E75.4.2.6", {"start": v(515.72, -68.7) * mm, "end": v(516.87, -66.7) * mm});
            skLineSegment(sketch, "E75.4.2.7", {"start": v(520.34, -68.7) * mm, "end": v(519.18, -70.7) * mm});
            skLineSegment(sketch, "E75.4.3.0", {"start": v(516.87, -72.05) * mm, "end": v(519.18, -72.05) * mm});
            skPoint(sketch, "E75.4.3.1", {"position": v(518.03, -72.05) * mm});
            skLineSegment(sketch, "E75.4.3.2", {"start": v(519.18, -72.05) * mm, "end": v(520.34, -74.05) * mm});
            skLineSegment(sketch, "E75.4.3.3", {"start": v(516.87, -76.05) * mm, "end": v(515.72, -74.05) * mm});
            skLineSegment(sketch, "E75.4.3.4", {"start": v(519.18, -76.05) * mm, "end": v(516.87, -76.05) * mm});
            skCircle(sketch, "E75.4.3.5", {"center": v(518.03, -74.05) * mm, "radius": 2 * mm, "construction": true});
            skLineSegment(sketch, "E75.4.3.6", {"start": v(515.72, -74.05) * mm, "end": v(516.87, -72.05) * mm});
            skLineSegment(sketch, "E75.4.3.7", {"start": v(520.34, -74.05) * mm, "end": v(519.18, -76.05) * mm});
            skLineSegment(sketch, "E75.4.4.0", {"start": v(516.87, -77.4) * mm, "end": v(519.18, -77.4) * mm});
            skPoint(sketch, "E75.4.4.1", {"position": v(518.03, -77.4) * mm});
            skLineSegment(sketch, "E75.4.4.2", {"start": v(519.18, -77.4) * mm, "end": v(520.34, -79.4) * mm});
            skLineSegment(sketch, "E75.4.4.3", {"start": v(516.87, -81.4) * mm, "end": v(515.72, -79.4) * mm});
            skLineSegment(sketch, "E75.4.4.4", {"start": v(519.18, -81.4) * mm, "end": v(516.87, -81.4) * mm});
            skCircle(sketch, "E75.4.4.5", {"center": v(518.03, -79.4) * mm, "radius": 2 * mm, "construction": true});
            skLineSegment(sketch, "E75.4.4.6", {"start": v(515.72, -79.4) * mm, "end": v(516.87, -77.4) * mm});
            skLineSegment(sketch, "E75.4.4.7", {"start": v(520.34, -79.4) * mm, "end": v(519.18, -81.4) * mm});
            skLineSegment(sketch, "E75.4.5.0", {"start": v(516.87, -82.75) * mm, "end": v(519.18, -82.75) * mm});
            skPoint(sketch, "E75.4.5.1", {"position": v(518.03, -82.75) * mm});
            skLineSegment(sketch, "E75.4.5.2", {"start": v(519.18, -82.75) * mm, "end": v(520.34, -84.75) * mm});
            skLineSegment(sketch, "E75.4.5.3", {"start": v(516.87, -86.75) * mm, "end": v(515.72, -84.75) * mm});
            skLineSegment(sketch, "E75.4.5.4", {"start": v(519.18, -86.75) * mm, "end": v(516.87, -86.75) * mm});
            skCircle(sketch, "E75.4.5.5", {"center": v(518.03, -84.75) * mm, "radius": 2 * mm, "construction": true});
            skLineSegment(sketch, "E75.4.5.6", {"start": v(515.72, -84.75) * mm, "end": v(516.87, -82.75) * mm});
            skLineSegment(sketch, "E75.4.5.7", {"start": v(520.34, -84.75) * mm, "end": v(519.18, -86.75) * mm});
            skLineSegment(sketch, "E75.4.6.0", {"start": v(516.87, -88.1) * mm, "end": v(519.18, -88.1) * mm});
            skPoint(sketch, "E75.4.6.1", {"position": v(518.03, -88.1) * mm});
            skLineSegment(sketch, "E75.4.6.2", {"start": v(519.18, -88.1) * mm, "end": v(520.34, -90.1) * mm});
            skLineSegment(sketch, "E75.4.6.3", {"start": v(516.87, -92.1) * mm, "end": v(515.72, -90.1) * mm});
            skLineSegment(sketch, "E75.4.6.4", {"start": v(519.18, -92.1) * mm, "end": v(516.87, -92.1) * mm});
            skCircle(sketch, "E75.4.6.5", {"center": v(518.03, -90.1) * mm, "radius": 2 * mm, "construction": true});
            skLineSegment(sketch, "E75.4.6.6", {"start": v(515.72, -90.1) * mm, "end": v(516.87, -88.1) * mm});
            skLineSegment(sketch, "E75.4.6.7", {"start": v(520.34, -90.1) * mm, "end": v(519.18, -92.1) * mm});
            skLineSegment(sketch, "E75.5.0.0", {"start": v(522.22, -56) * mm, "end": v(524.53, -56) * mm});
            skPoint(sketch, "E75.5.0.1", {"position": v(523.38, -56) * mm});
            skLineSegment(sketch, "E75.5.0.2", {"start": v(524.53, -56) * mm, "end": v(525.69, -58) * mm});
            skLineSegment(sketch, "E75.5.0.3", {"start": v(522.22, -60) * mm, "end": v(521.07, -58) * mm});
            skLineSegment(sketch, "E75.5.0.4", {"start": v(524.53, -60) * mm, "end": v(522.22, -60) * mm});
            skCircle(sketch, "E75.5.0.5", {"center": v(523.38, -58) * mm, "radius": 2 * mm, "construction": true});
            skLineSegment(sketch, "E75.5.0.6", {"start": v(521.07, -58) * mm, "end": v(522.22, -56) * mm});
            skLineSegment(sketch, "E75.5.0.7", {"start": v(525.69, -58) * mm, "end": v(524.53, -60) * mm});
            skLineSegment(sketch, "E75.5.1.0", {"start": v(522.22, -61.35) * mm, "end": v(524.53, -61.35) * mm});
            skPoint(sketch, "E75.5.1.1", {"position": v(523.38, -61.35) * mm});
            skLineSegment(sketch, "E75.5.1.2", {"start": v(524.53, -61.35) * mm, "end": v(525.69, -63.35) * mm});
            skLineSegment(sketch, "E75.5.1.3", {"start": v(522.22, -65.35) * mm, "end": v(521.07, -63.35) * mm});
            skLineSegment(sketch, "E75.5.1.4", {"start": v(524.53, -65.35) * mm, "end": v(522.22, -65.35) * mm});
            skCircle(sketch, "E75.5.1.5", {"center": v(523.38, -63.35) * mm, "radius": 2 * mm, "construction": true});
            skLineSegment(sketch, "E75.5.1.6", {"start": v(521.07, -63.35) * mm, "end": v(522.22, -61.35) * mm});
            skLineSegment(sketch, "E75.5.1.7", {"start": v(525.69, -63.35) * mm, "end": v(524.53, -65.35) * mm});
            skLineSegment(sketch, "E75.5.2.0", {"start": v(522.22, -66.7) * mm, "end": v(524.53, -66.7) * mm});
            skPoint(sketch, "E75.5.2.1", {"position": v(523.38, -66.7) * mm});
            skLineSegment(sketch, "E75.5.2.2", {"start": v(524.53, -66.7) * mm, "end": v(525.69, -68.7) * mm});
            skLineSegment(sketch, "E75.5.2.3", {"start": v(522.22, -70.7) * mm, "end": v(521.07, -68.7) * mm});
            skLineSegment(sketch, "E75.5.2.4", {"start": v(524.53, -70.7) * mm, "end": v(522.22, -70.7) * mm});
            skCircle(sketch, "E75.5.2.5", {"center": v(523.38, -68.7) * mm, "radius": 2 * mm, "construction": true});
            skLineSegment(sketch, "E75.5.2.6", {"start": v(521.07, -68.7) * mm, "end": v(522.22, -66.7) * mm});
            skLineSegment(sketch, "E75.5.2.7", {"start": v(525.69, -68.7) * mm, "end": v(524.53, -70.7) * mm});
            skLineSegment(sketch, "E75.5.3.0", {"start": v(522.22, -72.05) * mm, "end": v(524.53, -72.05) * mm});
            skPoint(sketch, "E75.5.3.1", {"position": v(523.38, -72.05) * mm});
            skLineSegment(sketch, "E75.5.3.2", {"start": v(524.53, -72.05) * mm, "end": v(525.69, -74.05) * mm});
            skLineSegment(sketch, "E75.5.3.3", {"start": v(522.22, -76.05) * mm, "end": v(521.07, -74.05) * mm});
            skLineSegment(sketch, "E75.5.3.4", {"start": v(524.53, -76.05) * mm, "end": v(522.22, -76.05) * mm});
            skCircle(sketch, "E75.5.3.5", {"center": v(523.38, -74.05) * mm, "radius": 2 * mm, "construction": true});
            skLineSegment(sketch, "E75.5.3.6", {"start": v(521.07, -74.05) * mm, "end": v(522.22, -72.05) * mm});
            skLineSegment(sketch, "E75.5.3.7", {"start": v(525.69, -74.05) * mm, "end": v(524.53, -76.05) * mm});
            skLineSegment(sketch, "E75.5.4.0", {"start": v(522.22, -77.4) * mm, "end": v(524.53, -77.4) * mm});
            skPoint(sketch, "E75.5.4.1", {"position": v(523.38, -77.4) * mm});
            skLineSegment(sketch, "E75.5.4.2", {"start": v(524.53, -77.4) * mm, "end": v(525.69, -79.4) * mm});
            skLineSegment(sketch, "E75.5.4.3", {"start": v(522.22, -81.4) * mm, "end": v(521.07, -79.4) * mm});
            skLineSegment(sketch, "E75.5.4.4", {"start": v(524.53, -81.4) * mm, "end": v(522.22, -81.4) * mm});
            skCircle(sketch, "E75.5.4.5", {"center": v(523.38, -79.4) * mm, "radius": 2 * mm, "construction": true});
            skLineSegment(sketch, "E75.5.4.6", {"start": v(521.07, -79.4) * mm, "end": v(522.22, -77.4) * mm});
            skLineSegment(sketch, "E75.5.4.7", {"start": v(525.69, -79.4) * mm, "end": v(524.53, -81.4) * mm});
            skLineSegment(sketch, "E75.5.5.0", {"start": v(522.22, -82.75) * mm, "end": v(524.53, -82.75) * mm});
            skPoint(sketch, "E75.5.5.1", {"position": v(523.38, -82.75) * mm});
            skLineSegment(sketch, "E75.5.5.2", {"start": v(524.53, -82.75) * mm, "end": v(525.69, -84.75) * mm});
            skLineSegment(sketch, "E75.5.5.3", {"start": v(522.22, -86.75) * mm, "end": v(521.07, -84.75) * mm});
            skLineSegment(sketch, "E75.5.5.4", {"start": v(524.53, -86.75) * mm, "end": v(522.22, -86.75) * mm});
            skCircle(sketch, "E75.5.5.5", {"center": v(523.38, -84.75) * mm, "radius": 2 * mm, "construction": true});
            skLineSegment(sketch, "E75.5.5.6", {"start": v(521.07, -84.75) * mm, "end": v(522.22, -82.75) * mm});
            skLineSegment(sketch, "E75.5.5.7", {"start": v(525.69, -84.75) * mm, "end": v(524.53, -86.75) * mm});
            skLineSegment(sketch, "E75.5.6.0", {"start": v(522.22, -88.1) * mm, "end": v(524.53, -88.1) * mm});
            skPoint(sketch, "E75.5.6.1", {"position": v(523.38, -88.1) * mm});
            skLineSegment(sketch, "E75.5.6.2", {"start": v(524.53, -88.1) * mm, "end": v(525.69, -90.1) * mm});
            skLineSegment(sketch, "E75.5.6.3", {"start": v(522.22, -92.1) * mm, "end": v(521.07, -90.1) * mm});
            skLineSegment(sketch, "E75.5.6.4", {"start": v(524.53, -92.1) * mm, "end": v(522.22, -92.1) * mm});
            skCircle(sketch, "E75.5.6.5", {"center": v(523.38, -90.1) * mm, "radius": 2 * mm, "construction": true});
            skLineSegment(sketch, "E75.5.6.6", {"start": v(521.07, -90.1) * mm, "end": v(522.22, -88.1) * mm});
            skLineSegment(sketch, "E75.5.6.7", {"start": v(525.69, -90.1) * mm, "end": v(524.53, -92.1) * mm});
            skLineSegment(sketch, "E75.6.1.0", {"start": v(527.57, -61.35) * mm, "end": v(529.88, -61.35) * mm});
            skPoint(sketch, "E75.6.1.1", {"position": v(528.73, -61.35) * mm});
            skLineSegment(sketch, "E75.6.1.2", {"start": v(529.88, -61.35) * mm, "end": v(531.04, -63.35) * mm});
            skLineSegment(sketch, "E75.6.1.3", {"start": v(527.57, -65.35) * mm, "end": v(526.42, -63.35) * mm});
            skLineSegment(sketch, "E75.6.1.4", {"start": v(529.88, -65.35) * mm, "end": v(527.57, -65.35) * mm});
            skCircle(sketch, "E75.6.1.5", {"center": v(528.73, -63.35) * mm, "radius": 2 * mm, "construction": true});
            skLineSegment(sketch, "E75.6.1.6", {"start": v(526.42, -63.35) * mm, "end": v(527.57, -61.35) * mm});
            skLineSegment(sketch, "E75.6.1.7", {"start": v(531.04, -63.35) * mm, "end": v(529.88, -65.35) * mm});
            skLineSegment(sketch, "E75.6.2.0", {"start": v(527.57, -66.7) * mm, "end": v(529.88, -66.7) * mm});
            skPoint(sketch, "E75.6.2.1", {"position": v(528.73, -66.7) * mm});
            skLineSegment(sketch, "E75.6.2.2", {"start": v(529.88, -66.7) * mm, "end": v(531.04, -68.7) * mm});
            skLineSegment(sketch, "E75.6.2.3", {"start": v(527.57, -70.7) * mm, "end": v(526.42, -68.7) * mm});
            skLineSegment(sketch, "E75.6.2.4", {"start": v(529.88, -70.7) * mm, "end": v(527.57, -70.7) * mm});
            skCircle(sketch, "E75.6.2.5", {"center": v(528.73, -68.7) * mm, "radius": 2 * mm, "construction": true});
            skLineSegment(sketch, "E75.6.2.6", {"start": v(526.42, -68.7) * mm, "end": v(527.57, -66.7) * mm});
            skLineSegment(sketch, "E75.6.2.7", {"start": v(531.04, -68.7) * mm, "end": v(529.88, -70.7) * mm});
            skLineSegment(sketch, "E75.6.3.0", {"start": v(527.57, -72.05) * mm, "end": v(529.88, -72.05) * mm});
            skPoint(sketch, "E75.6.3.1", {"position": v(528.73, -72.05) * mm});
            skLineSegment(sketch, "E75.6.3.2", {"start": v(529.88, -72.05) * mm, "end": v(531.04, -74.05) * mm});
            skLineSegment(sketch, "E75.6.3.3", {"start": v(527.57, -76.05) * mm, "end": v(526.42, -74.05) * mm});
            skLineSegment(sketch, "E75.6.3.4", {"start": v(529.88, -76.05) * mm, "end": v(527.57, -76.05) * mm});
            skCircle(sketch, "E75.6.3.5", {"center": v(528.73, -74.05) * mm, "radius": 2 * mm, "construction": true});
            skLineSegment(sketch, "E75.6.3.6", {"start": v(526.42, -74.05) * mm, "end": v(527.57, -72.05) * mm});
            skLineSegment(sketch, "E75.6.3.7", {"start": v(531.04, -74.05) * mm, "end": v(529.88, -76.05) * mm});
            skLineSegment(sketch, "E75.6.4.0", {"start": v(527.57, -77.4) * mm, "end": v(529.88, -77.4) * mm});
            skPoint(sketch, "E75.6.4.1", {"position": v(528.73, -77.4) * mm});
            skLineSegment(sketch, "E75.6.4.2", {"start": v(529.88, -77.4) * mm, "end": v(531.04, -79.4) * mm});
            skLineSegment(sketch, "E75.6.4.3", {"start": v(527.57, -81.4) * mm, "end": v(526.42, -79.4) * mm});
            skLineSegment(sketch, "E75.6.4.4", {"start": v(529.88, -81.4) * mm, "end": v(527.57, -81.4) * mm});
            skCircle(sketch, "E75.6.4.5", {"center": v(528.73, -79.4) * mm, "radius": 2 * mm, "construction": true});
            skLineSegment(sketch, "E75.6.4.6", {"start": v(526.42, -79.4) * mm, "end": v(527.57, -77.4) * mm});
            skLineSegment(sketch, "E75.6.4.7", {"start": v(531.04, -79.4) * mm, "end": v(529.88, -81.4) * mm});
            skLineSegment(sketch, "E75.6.5.0", {"start": v(527.57, -82.75) * mm, "end": v(529.88, -82.75) * mm});
            skPoint(sketch, "E75.6.5.1", {"position": v(528.73, -82.75) * mm});
            skLineSegment(sketch, "E75.6.5.2", {"start": v(529.88, -82.75) * mm, "end": v(531.04, -84.75) * mm});
            skLineSegment(sketch, "E75.6.5.3", {"start": v(527.57, -86.75) * mm, "end": v(526.42, -84.75) * mm});
            skLineSegment(sketch, "E75.6.5.4", {"start": v(529.88, -86.75) * mm, "end": v(527.57, -86.75) * mm});
            skCircle(sketch, "E75.6.5.5", {"center": v(528.73, -84.75) * mm, "radius": 2 * mm, "construction": true});
            skLineSegment(sketch, "E75.6.5.6", {"start": v(526.42, -84.75) * mm, "end": v(527.57, -82.75) * mm});
            skLineSegment(sketch, "E75.6.5.7", {"start": v(531.04, -84.75) * mm, "end": v(529.88, -86.75) * mm});
            skLineSegment(sketch, "E75.direction1", {"start": v(495.47, -60) * mm, "end": v(500.82, -60) * mm, "construction": true});
            skLineSegment(sketch, "E75.direction2", {"start": v(495.47, -60) * mm, "end": v(495.47, -65.35) * mm, "construction": true});
            skLineSegment(sketch, "E76.0.1.0", {"start": v(549.76, -65.66) * mm, "end": v(547.76, -64.5) * mm});
            skLineSegment(sketch, "E76.0.1.1", {"start": v(547.76, -64.5) * mm, "end": v(547.76, -62.2) * mm});
            skLineSegment(sketch, "E76.0.1.2", {"start": v(547.76, -62.2) * mm, "end": v(549.76, -61.04) * mm});
            skLineSegment(sketch, "E76.0.1.3", {"start": v(549.76, -61.04) * mm, "end": v(551.76, -62.2) * mm});
            skLineSegment(sketch, "E76.0.1.4", {"start": v(551.76, -64.5) * mm, "end": v(549.76, -65.66) * mm});
            skLineSegment(sketch, "E76.0.1.5", {"start": v(551.76, -62.2) * mm, "end": v(551.76, -64.5) * mm});
            skCircle(sketch, "E76.0.1.6", {"center": v(549.76, -63.35) * mm, "radius": 2 * mm, "construction": true});
            skPoint(sketch, "E76.0.1.7", {"position": v(551.76, -63.35) * mm});
            skLineSegment(sketch, "E76.0.2.0", {"start": v(549.76, -71) * mm, "end": v(547.76, -69.85) * mm});
            skLineSegment(sketch, "E76.0.2.1", {"start": v(547.76, -69.85) * mm, "end": v(547.76, -67.55) * mm});
            skLineSegment(sketch, "E76.0.2.2", {"start": v(547.76, -67.55) * mm, "end": v(549.76, -66.4) * mm});
            skLineSegment(sketch, "E76.0.2.3", {"start": v(549.76, -66.4) * mm, "end": v(551.76, -67.55) * mm});
            skLineSegment(sketch, "E76.0.2.4", {"start": v(551.76, -69.85) * mm, "end": v(549.76, -71) * mm});
            skLineSegment(sketch, "E76.0.2.5", {"start": v(551.76, -67.55) * mm, "end": v(551.76, -69.85) * mm});
            skCircle(sketch, "E76.0.2.6", {"center": v(549.76, -68.7) * mm, "radius": 2 * mm, "construction": true});
            skPoint(sketch, "E76.0.2.7", {"position": v(551.76, -68.7) * mm});
            skLineSegment(sketch, "E76.0.3.0", {"start": v(549.76, -76.36) * mm, "end": v(547.76, -75.2) * mm});
            skLineSegment(sketch, "E76.0.3.1", {"start": v(547.76, -75.2) * mm, "end": v(547.76, -72.9) * mm});
            skLineSegment(sketch, "E76.0.3.2", {"start": v(547.76, -72.9) * mm, "end": v(549.76, -71.74) * mm});
            skLineSegment(sketch, "E76.0.3.3", {"start": v(549.76, -71.74) * mm, "end": v(551.76, -72.9) * mm});
            skLineSegment(sketch, "E76.0.3.4", {"start": v(551.76, -75.2) * mm, "end": v(549.76, -76.36) * mm});
            skLineSegment(sketch, "E76.0.3.5", {"start": v(551.76, -72.9) * mm, "end": v(551.76, -75.2) * mm});
            skCircle(sketch, "E76.0.3.6", {"center": v(549.76, -74.05) * mm, "radius": 2 * mm, "construction": true});
            skPoint(sketch, "E76.0.3.7", {"position": v(551.76, -74.05) * mm});
            skLineSegment(sketch, "E76.0.4.0", {"start": v(549.76, -81.7) * mm, "end": v(547.76, -80.55) * mm});
            skLineSegment(sketch, "E76.0.4.1", {"start": v(547.76, -80.55) * mm, "end": v(547.76, -78.25) * mm});
            skLineSegment(sketch, "E76.0.4.2", {"start": v(547.76, -78.25) * mm, "end": v(549.76, -77.1) * mm});
            skLineSegment(sketch, "E76.0.4.3", {"start": v(549.76, -77.1) * mm, "end": v(551.76, -78.25) * mm});
            skLineSegment(sketch, "E76.0.4.4", {"start": v(551.76, -80.55) * mm, "end": v(549.76, -81.7) * mm});
            skLineSegment(sketch, "E76.0.4.5", {"start": v(551.76, -78.25) * mm, "end": v(551.76, -80.55) * mm});
            skCircle(sketch, "E76.0.4.6", {"center": v(549.76, -79.4) * mm, "radius": 2 * mm, "construction": true});
            skPoint(sketch, "E76.0.4.7", {"position": v(551.76, -79.4) * mm});
            skLineSegment(sketch, "E76.0.5.0", {"start": v(549.76, -87.06) * mm, "end": v(547.76, -85.9) * mm});
            skLineSegment(sketch, "E76.0.5.1", {"start": v(547.76, -85.9) * mm, "end": v(547.76, -83.6) * mm});
            skLineSegment(sketch, "E76.0.5.2", {"start": v(547.76, -83.6) * mm, "end": v(549.76, -82.44) * mm});
            skLineSegment(sketch, "E76.0.5.3", {"start": v(549.76, -82.44) * mm, "end": v(551.76, -83.6) * mm});
            skLineSegment(sketch, "E76.0.5.4", {"start": v(551.76, -85.9) * mm, "end": v(549.76, -87.06) * mm});
            skLineSegment(sketch, "E76.0.5.5", {"start": v(551.76, -83.6) * mm, "end": v(551.76, -85.9) * mm});
            skCircle(sketch, "E76.0.5.6", {"center": v(549.76, -84.75) * mm, "radius": 2 * mm, "construction": true});
            skPoint(sketch, "E76.0.5.7", {"position": v(551.76, -84.75) * mm});
            skLineSegment(sketch, "E76.1.0.0", {"start": v(555.11, -60.3) * mm, "end": v(553.11, -59.15) * mm});
            skLineSegment(sketch, "E76.1.0.1", {"start": v(553.11, -59.15) * mm, "end": v(553.11, -56.85) * mm});
            skLineSegment(sketch, "E76.1.0.2", {"start": v(553.11, -56.85) * mm, "end": v(555.11, -55.7) * mm});
            skLineSegment(sketch, "E76.1.0.3", {"start": v(555.11, -55.7) * mm, "end": v(557.11, -56.85) * mm});
            skLineSegment(sketch, "E76.1.0.4", {"start": v(557.11, -59.15) * mm, "end": v(555.11, -60.3) * mm});
            skLineSegment(sketch, "E76.1.0.5", {"start": v(557.11, -56.85) * mm, "end": v(557.11, -59.15) * mm});
            skCircle(sketch, "E76.1.0.6", {"center": v(555.11, -58) * mm, "radius": 2 * mm, "construction": true});
            skPoint(sketch, "E76.1.0.7", {"position": v(557.11, -58) * mm});
            skLineSegment(sketch, "E76.1.1.0", {"start": v(555.11, -65.66) * mm, "end": v(553.11, -64.5) * mm});
            skLineSegment(sketch, "E76.1.1.1", {"start": v(553.11, -64.5) * mm, "end": v(553.11, -62.2) * mm});
            skLineSegment(sketch, "E76.1.1.2", {"start": v(553.11, -62.2) * mm, "end": v(555.11, -61.04) * mm});
            skLineSegment(sketch, "E76.1.1.3", {"start": v(555.11, -61.04) * mm, "end": v(557.11, -62.2) * mm});
            skLineSegment(sketch, "E76.1.1.4", {"start": v(557.11, -64.5) * mm, "end": v(555.11, -65.66) * mm});
            skLineSegment(sketch, "E76.1.1.5", {"start": v(557.11, -62.2) * mm, "end": v(557.11, -64.5) * mm});
            skCircle(sketch, "E76.1.1.6", {"center": v(555.11, -63.35) * mm, "radius": 2 * mm, "construction": true});
            skPoint(sketch, "E76.1.1.7", {"position": v(557.11, -63.35) * mm});
            skLineSegment(sketch, "E76.1.2.0", {"start": v(555.11, -71) * mm, "end": v(553.11, -69.85) * mm});
            skLineSegment(sketch, "E76.1.2.1", {"start": v(553.11, -69.85) * mm, "end": v(553.11, -67.55) * mm});
            skLineSegment(sketch, "E76.1.2.2", {"start": v(553.11, -67.55) * mm, "end": v(555.11, -66.4) * mm});
            skLineSegment(sketch, "E76.1.2.3", {"start": v(555.11, -66.4) * mm, "end": v(557.11, -67.55) * mm});
            skLineSegment(sketch, "E76.1.2.4", {"start": v(557.11, -69.85) * mm, "end": v(555.11, -71) * mm});
            skLineSegment(sketch, "E76.1.2.5", {"start": v(557.11, -67.55) * mm, "end": v(557.11, -69.85) * mm});
            skCircle(sketch, "E76.1.2.6", {"center": v(555.11, -68.7) * mm, "radius": 2 * mm, "construction": true});
            skPoint(sketch, "E76.1.2.7", {"position": v(557.11, -68.7) * mm});
            skLineSegment(sketch, "E76.1.3.0", {"start": v(555.11, -76.36) * mm, "end": v(553.11, -75.2) * mm});
            skLineSegment(sketch, "E76.1.3.1", {"start": v(553.11, -75.2) * mm, "end": v(553.11, -72.9) * mm});
            skLineSegment(sketch, "E76.1.3.2", {"start": v(553.11, -72.9) * mm, "end": v(555.11, -71.74) * mm});
            skLineSegment(sketch, "E76.1.3.3", {"start": v(555.11, -71.74) * mm, "end": v(557.11, -72.9) * mm});
            skLineSegment(sketch, "E76.1.3.4", {"start": v(557.11, -75.2) * mm, "end": v(555.11, -76.36) * mm});
            skLineSegment(sketch, "E76.1.3.5", {"start": v(557.11, -72.9) * mm, "end": v(557.11, -75.2) * mm});
            skCircle(sketch, "E76.1.3.6", {"center": v(555.11, -74.05) * mm, "radius": 2 * mm, "construction": true});
            skPoint(sketch, "E76.1.3.7", {"position": v(557.11, -74.05) * mm});
            skLineSegment(sketch, "E76.1.4.0", {"start": v(555.11, -81.7) * mm, "end": v(553.11, -80.55) * mm});
            skLineSegment(sketch, "E76.1.4.1", {"start": v(553.11, -80.55) * mm, "end": v(553.11, -78.25) * mm});
            skLineSegment(sketch, "E76.1.4.2", {"start": v(553.11, -78.25) * mm, "end": v(555.11, -77.1) * mm});
            skLineSegment(sketch, "E76.1.4.3", {"start": v(555.11, -77.1) * mm, "end": v(557.11, -78.25) * mm});
            skLineSegment(sketch, "E76.1.4.4", {"start": v(557.11, -80.55) * mm, "end": v(555.11, -81.7) * mm});
            skLineSegment(sketch, "E76.1.4.5", {"start": v(557.11, -78.25) * mm, "end": v(557.11, -80.55) * mm});
            skCircle(sketch, "E76.1.4.6", {"center": v(555.11, -79.4) * mm, "radius": 2 * mm, "construction": true});
            skPoint(sketch, "E76.1.4.7", {"position": v(557.11, -79.4) * mm});
            skLineSegment(sketch, "E76.1.5.0", {"start": v(555.11, -87.06) * mm, "end": v(553.11, -85.9) * mm});
            skLineSegment(sketch, "E76.1.5.1", {"start": v(553.11, -85.9) * mm, "end": v(553.11, -83.6) * mm});
            skLineSegment(sketch, "E76.1.5.2", {"start": v(553.11, -83.6) * mm, "end": v(555.11, -82.44) * mm});
            skLineSegment(sketch, "E76.1.5.3", {"start": v(555.11, -82.44) * mm, "end": v(557.11, -83.6) * mm});
            skLineSegment(sketch, "E76.1.5.4", {"start": v(557.11, -85.9) * mm, "end": v(555.11, -87.06) * mm});
            skLineSegment(sketch, "E76.1.5.5", {"start": v(557.11, -83.6) * mm, "end": v(557.11, -85.9) * mm});
            skCircle(sketch, "E76.1.5.6", {"center": v(555.11, -84.75) * mm, "radius": 2 * mm, "construction": true});
            skPoint(sketch, "E76.1.5.7", {"position": v(557.11, -84.75) * mm});
            skLineSegment(sketch, "E76.1.6.0", {"start": v(555.11, -92.4) * mm, "end": v(553.11, -91.25) * mm});
            skLineSegment(sketch, "E76.1.6.1", {"start": v(553.11, -91.25) * mm, "end": v(553.11, -88.95) * mm});
            skLineSegment(sketch, "E76.1.6.2", {"start": v(553.11, -88.95) * mm, "end": v(555.11, -87.8) * mm});
            skLineSegment(sketch, "E76.1.6.3", {"start": v(555.11, -87.8) * mm, "end": v(557.11, -88.95) * mm});
            skLineSegment(sketch, "E76.1.6.4", {"start": v(557.11, -91.25) * mm, "end": v(555.11, -92.4) * mm});
            skLineSegment(sketch, "E76.1.6.5", {"start": v(557.11, -88.95) * mm, "end": v(557.11, -91.25) * mm});
            skCircle(sketch, "E76.1.6.6", {"center": v(555.11, -90.1) * mm, "radius": 2 * mm, "construction": true});
            skPoint(sketch, "E76.1.6.7", {"position": v(557.11, -90.1) * mm});
            skLineSegment(sketch, "E76.2.0.0", {"start": v(560.46, -60.3) * mm, "end": v(558.46, -59.15) * mm});
            skLineSegment(sketch, "E76.2.0.1", {"start": v(558.46, -59.15) * mm, "end": v(558.46, -56.85) * mm});
            skLineSegment(sketch, "E76.2.0.2", {"start": v(558.46, -56.85) * mm, "end": v(560.46, -55.7) * mm});
            skLineSegment(sketch, "E76.2.0.3", {"start": v(560.46, -55.7) * mm, "end": v(562.46, -56.85) * mm});
            skLineSegment(sketch, "E76.2.0.4", {"start": v(562.46, -59.15) * mm, "end": v(560.46, -60.3) * mm});
            skLineSegment(sketch, "E76.2.0.5", {"start": v(562.46, -56.85) * mm, "end": v(562.46, -59.15) * mm});
            skCircle(sketch, "E76.2.0.6", {"center": v(560.46, -58) * mm, "radius": 2 * mm, "construction": true});
            skPoint(sketch, "E76.2.0.7", {"position": v(562.46, -58) * mm});
            skLineSegment(sketch, "E76.2.1.0", {"start": v(560.46, -65.66) * mm, "end": v(558.46, -64.5) * mm});
            skLineSegment(sketch, "E76.2.1.1", {"start": v(558.46, -64.5) * mm, "end": v(558.46, -62.2) * mm});
            skLineSegment(sketch, "E76.2.1.2", {"start": v(558.46, -62.2) * mm, "end": v(560.46, -61.04) * mm});
            skLineSegment(sketch, "E76.2.1.3", {"start": v(560.46, -61.04) * mm, "end": v(562.46, -62.2) * mm});
            skLineSegment(sketch, "E76.2.1.4", {"start": v(562.46, -64.5) * mm, "end": v(560.46, -65.66) * mm});
            skLineSegment(sketch, "E76.2.1.5", {"start": v(562.46, -62.2) * mm, "end": v(562.46, -64.5) * mm});
            skCircle(sketch, "E76.2.1.6", {"center": v(560.46, -63.35) * mm, "radius": 2 * mm, "construction": true});
            skPoint(sketch, "E76.2.1.7", {"position": v(562.46, -63.35) * mm});
            skLineSegment(sketch, "E76.2.2.0", {"start": v(560.46, -71) * mm, "end": v(558.46, -69.85) * mm});
            skLineSegment(sketch, "E76.2.2.1", {"start": v(558.46, -69.85) * mm, "end": v(558.46, -67.55) * mm});
            skLineSegment(sketch, "E76.2.2.2", {"start": v(558.46, -67.55) * mm, "end": v(560.46, -66.4) * mm});
            skLineSegment(sketch, "E76.2.2.3", {"start": v(560.46, -66.4) * mm, "end": v(562.46, -67.55) * mm});
            skLineSegment(sketch, "E76.2.2.4", {"start": v(562.46, -69.85) * mm, "end": v(560.46, -71) * mm});
            skLineSegment(sketch, "E76.2.2.5", {"start": v(562.46, -67.55) * mm, "end": v(562.46, -69.85) * mm});
            skCircle(sketch, "E76.2.2.6", {"center": v(560.46, -68.7) * mm, "radius": 2 * mm, "construction": true});
            skPoint(sketch, "E76.2.2.7", {"position": v(562.46, -68.7) * mm});
            skLineSegment(sketch, "E76.2.3.0", {"start": v(560.46, -76.36) * mm, "end": v(558.46, -75.2) * mm});
            skLineSegment(sketch, "E76.2.3.1", {"start": v(558.46, -75.2) * mm, "end": v(558.46, -72.9) * mm});
            skLineSegment(sketch, "E76.2.3.2", {"start": v(558.46, -72.9) * mm, "end": v(560.46, -71.74) * mm});
            skLineSegment(sketch, "E76.2.3.3", {"start": v(560.46, -71.74) * mm, "end": v(562.46, -72.9) * mm});
            skLineSegment(sketch, "E76.2.3.4", {"start": v(562.46, -75.2) * mm, "end": v(560.46, -76.36) * mm});
            skLineSegment(sketch, "E76.2.3.5", {"start": v(562.46, -72.9) * mm, "end": v(562.46, -75.2) * mm});
            skCircle(sketch, "E76.2.3.6", {"center": v(560.46, -74.05) * mm, "radius": 2 * mm, "construction": true});
            skPoint(sketch, "E76.2.3.7", {"position": v(562.46, -74.05) * mm});
            skLineSegment(sketch, "E76.2.4.0", {"start": v(560.46, -81.7) * mm, "end": v(558.46, -80.55) * mm});
            skLineSegment(sketch, "E76.2.4.1", {"start": v(558.46, -80.55) * mm, "end": v(558.46, -78.25) * mm});
            skLineSegment(sketch, "E76.2.4.2", {"start": v(558.46, -78.25) * mm, "end": v(560.46, -77.1) * mm});
            skLineSegment(sketch, "E76.2.4.3", {"start": v(560.46, -77.1) * mm, "end": v(562.46, -78.25) * mm});
            skLineSegment(sketch, "E76.2.4.4", {"start": v(562.46, -80.55) * mm, "end": v(560.46, -81.7) * mm});
            skLineSegment(sketch, "E76.2.4.5", {"start": v(562.46, -78.25) * mm, "end": v(562.46, -80.55) * mm});
            skCircle(sketch, "E76.2.4.6", {"center": v(560.46, -79.4) * mm, "radius": 2 * mm, "construction": true});
            skPoint(sketch, "E76.2.4.7", {"position": v(562.46, -79.4) * mm});
            skLineSegment(sketch, "E76.2.5.0", {"start": v(560.46, -87.06) * mm, "end": v(558.46, -85.9) * mm});
            skLineSegment(sketch, "E76.2.5.1", {"start": v(558.46, -85.9) * mm, "end": v(558.46, -83.6) * mm});
            skLineSegment(sketch, "E76.2.5.2", {"start": v(558.46, -83.6) * mm, "end": v(560.46, -82.44) * mm});
            skLineSegment(sketch, "E76.2.5.3", {"start": v(560.46, -82.44) * mm, "end": v(562.46, -83.6) * mm});
            skLineSegment(sketch, "E76.2.5.4", {"start": v(562.46, -85.9) * mm, "end": v(560.46, -87.06) * mm});
            skLineSegment(sketch, "E76.2.5.5", {"start": v(562.46, -83.6) * mm, "end": v(562.46, -85.9) * mm});
            skCircle(sketch, "E76.2.5.6", {"center": v(560.46, -84.75) * mm, "radius": 2 * mm, "construction": true});
            skPoint(sketch, "E76.2.5.7", {"position": v(562.46, -84.75) * mm});
            skLineSegment(sketch, "E76.2.6.0", {"start": v(560.46, -92.4) * mm, "end": v(558.46, -91.25) * mm});
            skLineSegment(sketch, "E76.2.6.1", {"start": v(558.46, -91.25) * mm, "end": v(558.46, -88.95) * mm});
            skLineSegment(sketch, "E76.2.6.2", {"start": v(558.46, -88.95) * mm, "end": v(560.46, -87.8) * mm});
            skLineSegment(sketch, "E76.2.6.3", {"start": v(560.46, -87.8) * mm, "end": v(562.46, -88.95) * mm});
            skLineSegment(sketch, "E76.2.6.4", {"start": v(562.46, -91.25) * mm, "end": v(560.46, -92.4) * mm});
            skLineSegment(sketch, "E76.2.6.5", {"start": v(562.46, -88.95) * mm, "end": v(562.46, -91.25) * mm});
            skCircle(sketch, "E76.2.6.6", {"center": v(560.46, -90.1) * mm, "radius": 2 * mm, "construction": true});
            skPoint(sketch, "E76.2.6.7", {"position": v(562.46, -90.1) * mm});
            skLineSegment(sketch, "E76.3.0.0", {"start": v(565.81, -60.3) * mm, "end": v(563.81, -59.15) * mm});
            skLineSegment(sketch, "E76.3.0.1", {"start": v(563.81, -59.15) * mm, "end": v(563.81, -56.85) * mm});
            skLineSegment(sketch, "E76.3.0.2", {"start": v(563.81, -56.85) * mm, "end": v(565.81, -55.7) * mm});
            skLineSegment(sketch, "E76.3.0.3", {"start": v(565.81, -55.7) * mm, "end": v(567.81, -56.85) * mm});
            skLineSegment(sketch, "E76.3.0.4", {"start": v(567.81, -59.15) * mm, "end": v(565.81, -60.3) * mm});
            skLineSegment(sketch, "E76.3.0.5", {"start": v(567.81, -56.85) * mm, "end": v(567.81, -59.15) * mm});
            skCircle(sketch, "E76.3.0.6", {"center": v(565.81, -58) * mm, "radius": 2 * mm, "construction": true});
            skPoint(sketch, "E76.3.0.7", {"position": v(567.81, -58) * mm});
            skLineSegment(sketch, "E76.3.1.0", {"start": v(565.81, -65.66) * mm, "end": v(563.81, -64.5) * mm});
            skLineSegment(sketch, "E76.3.1.1", {"start": v(563.81, -64.5) * mm, "end": v(563.81, -62.2) * mm});
            skLineSegment(sketch, "E76.3.1.2", {"start": v(563.81, -62.2) * mm, "end": v(565.81, -61.04) * mm});
            skLineSegment(sketch, "E76.3.1.3", {"start": v(565.81, -61.04) * mm, "end": v(567.81, -62.2) * mm});
            skLineSegment(sketch, "E76.3.1.4", {"start": v(567.81, -64.5) * mm, "end": v(565.81, -65.66) * mm});
            skLineSegment(sketch, "E76.3.1.5", {"start": v(567.81, -62.2) * mm, "end": v(567.81, -64.5) * mm});
            skCircle(sketch, "E76.3.1.6", {"center": v(565.81, -63.35) * mm, "radius": 2 * mm, "construction": true});
            skPoint(sketch, "E76.3.1.7", {"position": v(567.81, -63.35) * mm});
            skLineSegment(sketch, "E76.3.2.0", {"start": v(565.81, -71) * mm, "end": v(563.81, -69.85) * mm});
            skLineSegment(sketch, "E76.3.2.1", {"start": v(563.81, -69.85) * mm, "end": v(563.81, -67.55) * mm});
            skLineSegment(sketch, "E76.3.2.2", {"start": v(563.81, -67.55) * mm, "end": v(565.81, -66.4) * mm});
            skLineSegment(sketch, "E76.3.2.3", {"start": v(565.81, -66.4) * mm, "end": v(567.81, -67.55) * mm});
            skLineSegment(sketch, "E76.3.2.4", {"start": v(567.81, -69.85) * mm, "end": v(565.81, -71) * mm});
            skLineSegment(sketch, "E76.3.2.5", {"start": v(567.81, -67.55) * mm, "end": v(567.81, -69.85) * mm});
            skCircle(sketch, "E76.3.2.6", {"center": v(565.81, -68.7) * mm, "radius": 2 * mm, "construction": true});
            skPoint(sketch, "E76.3.2.7", {"position": v(567.81, -68.7) * mm});
            skLineSegment(sketch, "E76.3.3.0", {"start": v(565.81, -76.36) * mm, "end": v(563.81, -75.2) * mm});
            skLineSegment(sketch, "E76.3.3.1", {"start": v(563.81, -75.2) * mm, "end": v(563.81, -72.9) * mm});
            skLineSegment(sketch, "E76.3.3.2", {"start": v(563.81, -72.9) * mm, "end": v(565.81, -71.74) * mm});
            skLineSegment(sketch, "E76.3.3.3", {"start": v(565.81, -71.74) * mm, "end": v(567.81, -72.9) * mm});
            skLineSegment(sketch, "E76.3.3.4", {"start": v(567.81, -75.2) * mm, "end": v(565.81, -76.36) * mm});
            skLineSegment(sketch, "E76.3.3.5", {"start": v(567.81, -72.9) * mm, "end": v(567.81, -75.2) * mm});
            skCircle(sketch, "E76.3.3.6", {"center": v(565.81, -74.05) * mm, "radius": 2 * mm, "construction": true});
            skPoint(sketch, "E76.3.3.7", {"position": v(567.81, -74.05) * mm});
            skLineSegment(sketch, "E76.3.4.0", {"start": v(565.81, -81.7) * mm, "end": v(563.81, -80.55) * mm});
            skLineSegment(sketch, "E76.3.4.1", {"start": v(563.81, -80.55) * mm, "end": v(563.81, -78.25) * mm});
            skLineSegment(sketch, "E76.3.4.2", {"start": v(563.81, -78.25) * mm, "end": v(565.81, -77.1) * mm});
            skLineSegment(sketch, "E76.3.4.3", {"start": v(565.81, -77.1) * mm, "end": v(567.81, -78.25) * mm});
            skLineSegment(sketch, "E76.3.4.4", {"start": v(567.81, -80.55) * mm, "end": v(565.81, -81.7) * mm});
            skLineSegment(sketch, "E76.3.4.5", {"start": v(567.81, -78.25) * mm, "end": v(567.81, -80.55) * mm});
            skCircle(sketch, "E76.3.4.6", {"center": v(565.81, -79.4) * mm, "radius": 2 * mm, "construction": true});
            skPoint(sketch, "E76.3.4.7", {"position": v(567.81, -79.4) * mm});
            skLineSegment(sketch, "E76.3.5.0", {"start": v(565.81, -87.06) * mm, "end": v(563.81, -85.9) * mm});
            skLineSegment(sketch, "E76.3.5.1", {"start": v(563.81, -85.9) * mm, "end": v(563.81, -83.6) * mm});
            skLineSegment(sketch, "E76.3.5.2", {"start": v(563.81, -83.6) * mm, "end": v(565.81, -82.44) * mm});
            skLineSegment(sketch, "E76.3.5.3", {"start": v(565.81, -82.44) * mm, "end": v(567.81, -83.6) * mm});
            skLineSegment(sketch, "E76.3.5.4", {"start": v(567.81, -85.9) * mm, "end": v(565.81, -87.06) * mm});
            skLineSegment(sketch, "E76.3.5.5", {"start": v(567.81, -83.6) * mm, "end": v(567.81, -85.9) * mm});
            skCircle(sketch, "E76.3.5.6", {"center": v(565.81, -84.75) * mm, "radius": 2 * mm, "construction": true});
            skPoint(sketch, "E76.3.5.7", {"position": v(567.81, -84.75) * mm});
            skLineSegment(sketch, "E76.3.6.0", {"start": v(565.81, -92.4) * mm, "end": v(563.81, -91.25) * mm});
            skLineSegment(sketch, "E76.3.6.1", {"start": v(563.81, -91.25) * mm, "end": v(563.81, -88.95) * mm});
            skLineSegment(sketch, "E76.3.6.2", {"start": v(563.81, -88.95) * mm, "end": v(565.81, -87.8) * mm});
            skLineSegment(sketch, "E76.3.6.3", {"start": v(565.81, -87.8) * mm, "end": v(567.81, -88.95) * mm});
            skLineSegment(sketch, "E76.3.6.4", {"start": v(567.81, -91.25) * mm, "end": v(565.81, -92.4) * mm});
            skLineSegment(sketch, "E76.3.6.5", {"start": v(567.81, -88.95) * mm, "end": v(567.81, -91.25) * mm});
            skCircle(sketch, "E76.3.6.6", {"center": v(565.81, -90.1) * mm, "radius": 2 * mm, "construction": true});
            skPoint(sketch, "E76.3.6.7", {"position": v(567.81, -90.1) * mm});
            skLineSegment(sketch, "E76.4.0.0", {"start": v(571.16, -60.3) * mm, "end": v(569.16, -59.15) * mm});
            skLineSegment(sketch, "E76.4.0.1", {"start": v(569.16, -59.15) * mm, "end": v(569.16, -56.85) * mm});
            skLineSegment(sketch, "E76.4.0.2", {"start": v(569.16, -56.85) * mm, "end": v(571.16, -55.7) * mm});
            skLineSegment(sketch, "E76.4.0.3", {"start": v(571.16, -55.7) * mm, "end": v(573.16, -56.85) * mm});
            skLineSegment(sketch, "E76.4.0.4", {"start": v(573.16, -59.15) * mm, "end": v(571.16, -60.3) * mm});
            skLineSegment(sketch, "E76.4.0.5", {"start": v(573.16, -56.85) * mm, "end": v(573.16, -59.15) * mm});
            skCircle(sketch, "E76.4.0.6", {"center": v(571.16, -58) * mm, "radius": 2 * mm, "construction": true});
            skPoint(sketch, "E76.4.0.7", {"position": v(573.16, -58) * mm});
            skLineSegment(sketch, "E76.4.1.0", {"start": v(571.16, -65.66) * mm, "end": v(569.16, -64.5) * mm});
            skLineSegment(sketch, "E76.4.1.1", {"start": v(569.16, -64.5) * mm, "end": v(569.16, -62.2) * mm});
            skLineSegment(sketch, "E76.4.1.2", {"start": v(569.16, -62.2) * mm, "end": v(571.16, -61.04) * mm});
            skLineSegment(sketch, "E76.4.1.3", {"start": v(571.16, -61.04) * mm, "end": v(573.16, -62.2) * mm});
            skLineSegment(sketch, "E76.4.1.4", {"start": v(573.16, -64.5) * mm, "end": v(571.16, -65.66) * mm});
            skLineSegment(sketch, "E76.4.1.5", {"start": v(573.16, -62.2) * mm, "end": v(573.16, -64.5) * mm});
            skCircle(sketch, "E76.4.1.6", {"center": v(571.16, -63.35) * mm, "radius": 2 * mm, "construction": true});
            skPoint(sketch, "E76.4.1.7", {"position": v(573.16, -63.35) * mm});
            skLineSegment(sketch, "E76.4.2.0", {"start": v(571.16, -71) * mm, "end": v(569.16, -69.85) * mm});
            skLineSegment(sketch, "E76.4.2.1", {"start": v(569.16, -69.85) * mm, "end": v(569.16, -67.55) * mm});
            skLineSegment(sketch, "E76.4.2.2", {"start": v(569.16, -67.55) * mm, "end": v(571.16, -66.4) * mm});
            skLineSegment(sketch, "E76.4.2.3", {"start": v(571.16, -66.4) * mm, "end": v(573.16, -67.55) * mm});
            skLineSegment(sketch, "E76.4.2.4", {"start": v(573.16, -69.85) * mm, "end": v(571.16, -71) * mm});
            skLineSegment(sketch, "E76.4.2.5", {"start": v(573.16, -67.55) * mm, "end": v(573.16, -69.85) * mm});
            skCircle(sketch, "E76.4.2.6", {"center": v(571.16, -68.7) * mm, "radius": 2 * mm, "construction": true});
            skPoint(sketch, "E76.4.2.7", {"position": v(573.16, -68.7) * mm});
            skLineSegment(sketch, "E76.4.3.0", {"start": v(571.16, -76.36) * mm, "end": v(569.16, -75.2) * mm});
            skLineSegment(sketch, "E76.4.3.1", {"start": v(569.16, -75.2) * mm, "end": v(569.16, -72.9) * mm});
            skLineSegment(sketch, "E76.4.3.2", {"start": v(569.16, -72.9) * mm, "end": v(571.16, -71.74) * mm});
            skLineSegment(sketch, "E76.4.3.3", {"start": v(571.16, -71.74) * mm, "end": v(573.16, -72.9) * mm});
            skLineSegment(sketch, "E76.4.3.4", {"start": v(573.16, -75.2) * mm, "end": v(571.16, -76.36) * mm});
            skLineSegment(sketch, "E76.4.3.5", {"start": v(573.16, -72.9) * mm, "end": v(573.16, -75.2) * mm});
            skCircle(sketch, "E76.4.3.6", {"center": v(571.16, -74.05) * mm, "radius": 2 * mm, "construction": true});
            skPoint(sketch, "E76.4.3.7", {"position": v(573.16, -74.05) * mm});
            skLineSegment(sketch, "E76.4.4.0", {"start": v(571.16, -81.7) * mm, "end": v(569.16, -80.55) * mm});
            skLineSegment(sketch, "E76.4.4.1", {"start": v(569.16, -80.55) * mm, "end": v(569.16, -78.25) * mm});
            skLineSegment(sketch, "E76.4.4.2", {"start": v(569.16, -78.25) * mm, "end": v(571.16, -77.1) * mm});
            skLineSegment(sketch, "E76.4.4.3", {"start": v(571.16, -77.1) * mm, "end": v(573.16, -78.25) * mm});
            skLineSegment(sketch, "E76.4.4.4", {"start": v(573.16, -80.55) * mm, "end": v(571.16, -81.7) * mm});
            skLineSegment(sketch, "E76.4.4.5", {"start": v(573.16, -78.25) * mm, "end": v(573.16, -80.55) * mm});
            skCircle(sketch, "E76.4.4.6", {"center": v(571.16, -79.4) * mm, "radius": 2 * mm, "construction": true});
            skPoint(sketch, "E76.4.4.7", {"position": v(573.16, -79.4) * mm});
            skLineSegment(sketch, "E76.4.5.0", {"start": v(571.16, -87.06) * mm, "end": v(569.16, -85.9) * mm});
            skLineSegment(sketch, "E76.4.5.1", {"start": v(569.16, -85.9) * mm, "end": v(569.16, -83.6) * mm});
            skLineSegment(sketch, "E76.4.5.2", {"start": v(569.16, -83.6) * mm, "end": v(571.16, -82.44) * mm});
            skLineSegment(sketch, "E76.4.5.3", {"start": v(571.16, -82.44) * mm, "end": v(573.16, -83.6) * mm});
            skLineSegment(sketch, "E76.4.5.4", {"start": v(573.16, -85.9) * mm, "end": v(571.16, -87.06) * mm});
            skLineSegment(sketch, "E76.4.5.5", {"start": v(573.16, -83.6) * mm, "end": v(573.16, -85.9) * mm});
            skCircle(sketch, "E76.4.5.6", {"center": v(571.16, -84.75) * mm, "radius": 2 * mm, "construction": true});
            skPoint(sketch, "E76.4.5.7", {"position": v(573.16, -84.75) * mm});
            skLineSegment(sketch, "E76.4.6.0", {"start": v(571.16, -92.4) * mm, "end": v(569.16, -91.25) * mm});
            skLineSegment(sketch, "E76.4.6.1", {"start": v(569.16, -91.25) * mm, "end": v(569.16, -88.95) * mm});
            skLineSegment(sketch, "E76.4.6.2", {"start": v(569.16, -88.95) * mm, "end": v(571.16, -87.8) * mm});
            skLineSegment(sketch, "E76.4.6.3", {"start": v(571.16, -87.8) * mm, "end": v(573.16, -88.95) * mm});
            skLineSegment(sketch, "E76.4.6.4", {"start": v(573.16, -91.25) * mm, "end": v(571.16, -92.4) * mm});
            skLineSegment(sketch, "E76.4.6.5", {"start": v(573.16, -88.95) * mm, "end": v(573.16, -91.25) * mm});
            skCircle(sketch, "E76.4.6.6", {"center": v(571.16, -90.1) * mm, "radius": 2 * mm, "construction": true});
            skPoint(sketch, "E76.4.6.7", {"position": v(573.16, -90.1) * mm});
            skLineSegment(sketch, "E76.5.0.0", {"start": v(576.51, -60.3) * mm, "end": v(574.51, -59.15) * mm});
            skLineSegment(sketch, "E76.5.0.1", {"start": v(574.51, -59.15) * mm, "end": v(574.51, -56.85) * mm});
            skLineSegment(sketch, "E76.5.0.2", {"start": v(574.51, -56.85) * mm, "end": v(576.51, -55.7) * mm});
            skLineSegment(sketch, "E76.5.0.3", {"start": v(576.51, -55.7) * mm, "end": v(578.51, -56.85) * mm});
            skLineSegment(sketch, "E76.5.0.4", {"start": v(578.51, -59.15) * mm, "end": v(576.51, -60.3) * mm});
            skLineSegment(sketch, "E76.5.0.5", {"start": v(578.51, -56.85) * mm, "end": v(578.51, -59.15) * mm});
            skCircle(sketch, "E76.5.0.6", {"center": v(576.51, -58) * mm, "radius": 2 * mm, "construction": true});
            skPoint(sketch, "E76.5.0.7", {"position": v(578.51, -58) * mm});
            skLineSegment(sketch, "E76.5.1.0", {"start": v(576.51, -65.66) * mm, "end": v(574.51, -64.5) * mm});
            skLineSegment(sketch, "E76.5.1.1", {"start": v(574.51, -64.5) * mm, "end": v(574.51, -62.2) * mm});
            skLineSegment(sketch, "E76.5.1.2", {"start": v(574.51, -62.2) * mm, "end": v(576.51, -61.04) * mm});
            skLineSegment(sketch, "E76.5.1.3", {"start": v(576.51, -61.04) * mm, "end": v(578.51, -62.2) * mm});
            skLineSegment(sketch, "E76.5.1.4", {"start": v(578.51, -64.5) * mm, "end": v(576.51, -65.66) * mm});
            skLineSegment(sketch, "E76.5.1.5", {"start": v(578.51, -62.2) * mm, "end": v(578.51, -64.5) * mm});
            skCircle(sketch, "E76.5.1.6", {"center": v(576.51, -63.35) * mm, "radius": 2 * mm, "construction": true});
            skPoint(sketch, "E76.5.1.7", {"position": v(578.51, -63.35) * mm});
            skLineSegment(sketch, "E76.5.2.0", {"start": v(576.51, -71) * mm, "end": v(574.51, -69.85) * mm});
            skLineSegment(sketch, "E76.5.2.1", {"start": v(574.51, -69.85) * mm, "end": v(574.51, -67.55) * mm});
            skLineSegment(sketch, "E76.5.2.2", {"start": v(574.51, -67.55) * mm, "end": v(576.51, -66.4) * mm});
            skLineSegment(sketch, "E76.5.2.3", {"start": v(576.51, -66.4) * mm, "end": v(578.51, -67.55) * mm});
            skLineSegment(sketch, "E76.5.2.4", {"start": v(578.51, -69.85) * mm, "end": v(576.51, -71) * mm});
            skLineSegment(sketch, "E76.5.2.5", {"start": v(578.51, -67.55) * mm, "end": v(578.51, -69.85) * mm});
            skCircle(sketch, "E76.5.2.6", {"center": v(576.51, -68.7) * mm, "radius": 2 * mm, "construction": true});
            skPoint(sketch, "E76.5.2.7", {"position": v(578.51, -68.7) * mm});
            skLineSegment(sketch, "E76.5.3.0", {"start": v(576.51, -76.36) * mm, "end": v(574.51, -75.2) * mm});
            skLineSegment(sketch, "E76.5.3.1", {"start": v(574.51, -75.2) * mm, "end": v(574.51, -72.9) * mm});
            skLineSegment(sketch, "E76.5.3.2", {"start": v(574.51, -72.9) * mm, "end": v(576.51, -71.74) * mm});
            skLineSegment(sketch, "E76.5.3.3", {"start": v(576.51, -71.74) * mm, "end": v(578.51, -72.9) * mm});
            skLineSegment(sketch, "E76.5.3.4", {"start": v(578.51, -75.2) * mm, "end": v(576.51, -76.36) * mm});
            skLineSegment(sketch, "E76.5.3.5", {"start": v(578.51, -72.9) * mm, "end": v(578.51, -75.2) * mm});
            skCircle(sketch, "E76.5.3.6", {"center": v(576.51, -74.05) * mm, "radius": 2 * mm, "construction": true});
            skPoint(sketch, "E76.5.3.7", {"position": v(578.51, -74.05) * mm});
            skLineSegment(sketch, "E76.5.4.0", {"start": v(576.51, -81.7) * mm, "end": v(574.51, -80.55) * mm});
            skLineSegment(sketch, "E76.5.4.1", {"start": v(574.51, -80.55) * mm, "end": v(574.51, -78.25) * mm});
            skLineSegment(sketch, "E76.5.4.2", {"start": v(574.51, -78.25) * mm, "end": v(576.51, -77.1) * mm});
            skLineSegment(sketch, "E76.5.4.3", {"start": v(576.51, -77.1) * mm, "end": v(578.51, -78.25) * mm});
            skLineSegment(sketch, "E76.5.4.4", {"start": v(578.51, -80.55) * mm, "end": v(576.51, -81.7) * mm});
            skLineSegment(sketch, "E76.5.4.5", {"start": v(578.51, -78.25) * mm, "end": v(578.51, -80.55) * mm});
            skCircle(sketch, "E76.5.4.6", {"center": v(576.51, -79.4) * mm, "radius": 2 * mm, "construction": true});
            skPoint(sketch, "E76.5.4.7", {"position": v(578.51, -79.4) * mm});
            skLineSegment(sketch, "E76.5.5.0", {"start": v(576.51, -87.06) * mm, "end": v(574.51, -85.9) * mm});
            skLineSegment(sketch, "E76.5.5.1", {"start": v(574.51, -85.9) * mm, "end": v(574.51, -83.6) * mm});
            skLineSegment(sketch, "E76.5.5.2", {"start": v(574.51, -83.6) * mm, "end": v(576.51, -82.44) * mm});
            skLineSegment(sketch, "E76.5.5.3", {"start": v(576.51, -82.44) * mm, "end": v(578.51, -83.6) * mm});
            skLineSegment(sketch, "E76.5.5.4", {"start": v(578.51, -85.9) * mm, "end": v(576.51, -87.06) * mm});
            skLineSegment(sketch, "E76.5.5.5", {"start": v(578.51, -83.6) * mm, "end": v(578.51, -85.9) * mm});
            skCircle(sketch, "E76.5.5.6", {"center": v(576.51, -84.75) * mm, "radius": 2 * mm, "construction": true});
            skPoint(sketch, "E76.5.5.7", {"position": v(578.51, -84.75) * mm});
            skLineSegment(sketch, "E76.5.6.0", {"start": v(576.51, -92.4) * mm, "end": v(574.51, -91.25) * mm});
            skLineSegment(sketch, "E76.5.6.1", {"start": v(574.51, -91.25) * mm, "end": v(574.51, -88.95) * mm});
            skLineSegment(sketch, "E76.5.6.2", {"start": v(574.51, -88.95) * mm, "end": v(576.51, -87.8) * mm});
            skLineSegment(sketch, "E76.5.6.3", {"start": v(576.51, -87.8) * mm, "end": v(578.51, -88.95) * mm});
            skLineSegment(sketch, "E76.5.6.4", {"start": v(578.51, -91.25) * mm, "end": v(576.51, -92.4) * mm});
            skLineSegment(sketch, "E76.5.6.5", {"start": v(578.51, -88.95) * mm, "end": v(578.51, -91.25) * mm});
            skCircle(sketch, "E76.5.6.6", {"center": v(576.51, -90.1) * mm, "radius": 2 * mm, "construction": true});
            skPoint(sketch, "E76.5.6.7", {"position": v(578.51, -90.1) * mm});
            skLineSegment(sketch, "E76.6.1.0", {"start": v(581.86, -65.66) * mm, "end": v(579.86, -64.5) * mm});
            skLineSegment(sketch, "E76.6.1.1", {"start": v(579.86, -64.5) * mm, "end": v(579.86, -62.2) * mm});
            skLineSegment(sketch, "E76.6.1.2", {"start": v(579.86, -62.2) * mm, "end": v(581.86, -61.04) * mm});
            skLineSegment(sketch, "E76.6.1.3", {"start": v(581.86, -61.04) * mm, "end": v(583.86, -62.2) * mm});
            skLineSegment(sketch, "E76.6.1.4", {"start": v(583.86, -64.5) * mm, "end": v(581.86, -65.66) * mm});
            skLineSegment(sketch, "E76.6.1.5", {"start": v(583.86, -62.2) * mm, "end": v(583.86, -64.5) * mm});
            skCircle(sketch, "E76.6.1.6", {"center": v(581.86, -63.35) * mm, "radius": 2 * mm, "construction": true});
            skPoint(sketch, "E76.6.1.7", {"position": v(583.86, -63.35) * mm});
            skLineSegment(sketch, "E76.6.2.0", {"start": v(581.86, -71) * mm, "end": v(579.86, -69.85) * mm});
            skLineSegment(sketch, "E76.6.2.1", {"start": v(579.86, -69.85) * mm, "end": v(579.86, -67.55) * mm});
            skLineSegment(sketch, "E76.6.2.2", {"start": v(579.86, -67.55) * mm, "end": v(581.86, -66.4) * mm});
            skLineSegment(sketch, "E76.6.2.3", {"start": v(581.86, -66.4) * mm, "end": v(583.86, -67.55) * mm});
            skLineSegment(sketch, "E76.6.2.4", {"start": v(583.86, -69.85) * mm, "end": v(581.86, -71) * mm});
            skLineSegment(sketch, "E76.6.2.5", {"start": v(583.86, -67.55) * mm, "end": v(583.86, -69.85) * mm});
            skCircle(sketch, "E76.6.2.6", {"center": v(581.86, -68.7) * mm, "radius": 2 * mm, "construction": true});
            skPoint(sketch, "E76.6.2.7", {"position": v(583.86, -68.7) * mm});
            skLineSegment(sketch, "E76.6.3.0", {"start": v(581.86, -76.36) * mm, "end": v(579.86, -75.2) * mm});
            skLineSegment(sketch, "E76.6.3.1", {"start": v(579.86, -75.2) * mm, "end": v(579.86, -72.9) * mm});
            skLineSegment(sketch, "E76.6.3.2", {"start": v(579.86, -72.9) * mm, "end": v(581.86, -71.74) * mm});
            skLineSegment(sketch, "E76.6.3.3", {"start": v(581.86, -71.74) * mm, "end": v(583.86, -72.9) * mm});
            skLineSegment(sketch, "E76.6.3.4", {"start": v(583.86, -75.2) * mm, "end": v(581.86, -76.36) * mm});
            skLineSegment(sketch, "E76.6.3.5", {"start": v(583.86, -72.9) * mm, "end": v(583.86, -75.2) * mm});
            skCircle(sketch, "E76.6.3.6", {"center": v(581.86, -74.05) * mm, "radius": 2 * mm, "construction": true});
            skPoint(sketch, "E76.6.3.7", {"position": v(583.86, -74.05) * mm});
            skLineSegment(sketch, "E76.6.4.0", {"start": v(581.86, -81.7) * mm, "end": v(579.86, -80.55) * mm});
            skLineSegment(sketch, "E76.6.4.1", {"start": v(579.86, -80.55) * mm, "end": v(579.86, -78.25) * mm});
            skLineSegment(sketch, "E76.6.4.2", {"start": v(579.86, -78.25) * mm, "end": v(581.86, -77.1) * mm});
            skLineSegment(sketch, "E76.6.4.3", {"start": v(581.86, -77.1) * mm, "end": v(583.86, -78.25) * mm});
            skLineSegment(sketch, "E76.6.4.4", {"start": v(583.86, -80.55) * mm, "end": v(581.86, -81.7) * mm});
            skLineSegment(sketch, "E76.6.4.5", {"start": v(583.86, -78.25) * mm, "end": v(583.86, -80.55) * mm});
            skCircle(sketch, "E76.6.4.6", {"center": v(581.86, -79.4) * mm, "radius": 2 * mm, "construction": true});
            skPoint(sketch, "E76.6.4.7", {"position": v(583.86, -79.4) * mm});
            skLineSegment(sketch, "E76.6.5.0", {"start": v(581.86, -87.06) * mm, "end": v(579.86, -85.9) * mm});
            skLineSegment(sketch, "E76.6.5.1", {"start": v(579.86, -85.9) * mm, "end": v(579.86, -83.6) * mm});
            skLineSegment(sketch, "E76.6.5.2", {"start": v(579.86, -83.6) * mm, "end": v(581.86, -82.44) * mm});
            skLineSegment(sketch, "E76.6.5.3", {"start": v(581.86, -82.44) * mm, "end": v(583.86, -83.6) * mm});
            skLineSegment(sketch, "E76.6.5.4", {"start": v(583.86, -85.9) * mm, "end": v(581.86, -87.06) * mm});
            skLineSegment(sketch, "E76.6.5.5", {"start": v(583.86, -83.6) * mm, "end": v(583.86, -85.9) * mm});
            skCircle(sketch, "E76.6.5.6", {"center": v(581.86, -84.75) * mm, "radius": 2 * mm, "construction": true});
            skPoint(sketch, "E76.6.5.7", {"position": v(583.86, -84.75) * mm});
            skLineSegment(sketch, "E76.direction1", {"start": v(547.76, -59.15) * mm, "end": v(553.11, -59.15) * mm, "construction": true});
            skLineSegment(sketch, "E76.direction2", {"start": v(547.76, -59.15) * mm, "end": v(547.76, -64.5) * mm, "construction": true});
            skLineSegment(sketch, "E77", {"start": v(-134.56, -91.36) * mm, "end": v(821.77, -91.36) * mm, "construction": true});
            skLineSegment(sketch, "E78", {"start": v(-239, -184.73) * mm, "end": v(-239, -119.54) * mm});
            skLineSegment(sketch, "E79", {"start": v(-239, -119.54) * mm, "end": v(-235, -119.54) * mm});
            skLineSegment(sketch, "E80.bottom", {"start": v(-148.85, -125.01) * mm, "end": v(-135.85, -125.01) * mm});
            skLineSegment(sketch, "E80.top", {"start": v(-148.85, -131.01) * mm, "end": v(-135.85, -131.01) * mm});
            skLineSegment(sketch, "E80.left", {"start": v(-148.85, -125.01) * mm, "end": v(-148.85, -131.01) * mm});
            skLineSegment(sketch, "E80.right", {"start": v(-135.85, -125.01) * mm, "end": v(-135.85, -131.01) * mm});
            skLineSegment(sketch, "E81.bottom", {"start": v(-103.98, -124.48) * mm, "end": v(-90.98, -124.48) * mm});
            skLineSegment(sketch, "E81.top", {"start": v(-103.98, -130.48) * mm, "end": v(-90.98, -130.48) * mm});
            skLineSegment(sketch, "E81.left", {"start": v(-103.98, -124.48) * mm, "end": v(-103.98, -130.48) * mm});
            skLineSegment(sketch, "E81.right", {"start": v(-90.98, -124.48) * mm, "end": v(-90.98, -130.48) * mm});
            skLineSegment(sketch, "E82.bottom", {"start": v(-55.3, -124.85) * mm, "end": v(-42.3, -124.85) * mm});
            skLineSegment(sketch, "E82.top", {"start": v(-55.3, -130.85) * mm, "end": v(-42.3, -130.85) * mm});
            skLineSegment(sketch, "E82.left", {"start": v(-55.3, -124.85) * mm, "end": v(-55.3, -130.85) * mm});
            skLineSegment(sketch, "E82.right", {"start": v(-42.3, -124.85) * mm, "end": v(-42.3, -130.85) * mm});
            skLineSegment(sketch, "E83.bottom", {"start": v(-150.12, 2.08) * mm, "end": v(-137.12, 2.08) * mm});
            skLineSegment(sketch, "E83.top", {"start": v(-150.12, -3.92) * mm, "end": v(-137.12, -3.92) * mm});
            skLineSegment(sketch, "E83.left", {"start": v(-150.12, 2.08) * mm, "end": v(-150.12, -3.92) * mm});
            skLineSegment(sketch, "E83.right", {"start": v(-137.12, 2.08) * mm, "end": v(-137.12, -3.92) * mm});
            skLineSegment(sketch, "E84.bottom", {"start": v(-105.25, 2.62) * mm, "end": v(-92.25, 2.62) * mm});
            skLineSegment(sketch, "E84.top", {"start": v(-105.25, -3.38) * mm, "end": v(-92.25, -3.38) * mm});
            skLineSegment(sketch, "E84.left", {"start": v(-105.25, 2.62) * mm, "end": v(-105.25, -3.38) * mm});
            skLineSegment(sketch, "E84.right", {"start": v(-92.25, 2.62) * mm, "end": v(-92.25, -3.38) * mm});
            skLineSegment(sketch, "E85.bottom", {"start": v(-56.57, 2.24) * mm, "end": v(-43.57, 2.24) * mm});
            skLineSegment(sketch, "E85.top", {"start": v(-56.57, -3.76) * mm, "end": v(-43.57, -3.76) * mm});
            skLineSegment(sketch, "E85.left", {"start": v(-56.57, 2.24) * mm, "end": v(-56.57, -3.76) * mm});
            skLineSegment(sketch, "E85.right", {"start": v(-43.57, 2.24) * mm, "end": v(-43.57, -3.76) * mm});
            skLineSegment(sketch, "E86.bottom", {"start": v(-150.48, 111.6) * mm, "end": v(-137.48, 111.6) * mm});
            skLineSegment(sketch, "E86.top", {"start": v(-150.48, 105.6) * mm, "end": v(-137.48, 105.6) * mm});
            skLineSegment(sketch, "E86.left", {"start": v(-150.48, 111.6) * mm, "end": v(-150.48, 105.6) * mm});
            skLineSegment(sketch, "E86.right", {"start": v(-137.48, 111.6) * mm, "end": v(-137.48, 105.6) * mm});
            skLineSegment(sketch, "E87.bottom", {"start": v(-105.6, 112.13) * mm, "end": v(-92.6, 112.13) * mm});
            skLineSegment(sketch, "E87.top", {"start": v(-105.6, 106.13) * mm, "end": v(-92.6, 106.13) * mm});
            skLineSegment(sketch, "E87.left", {"start": v(-105.6, 112.13) * mm, "end": v(-105.6, 106.13) * mm});
            skLineSegment(sketch, "E87.right", {"start": v(-92.6, 112.13) * mm, "end": v(-92.6, 106.13) * mm});
            skLineSegment(sketch, "E88.bottom", {"start": v(-56.93, 111.75) * mm, "end": v(-43.93, 111.75) * mm});
            skLineSegment(sketch, "E88.top", {"start": v(-56.93, 105.75) * mm, "end": v(-43.93, 105.75) * mm});
            skLineSegment(sketch, "E88.left", {"start": v(-56.93, 111.75) * mm, "end": v(-56.93, 105.75) * mm});
            skLineSegment(sketch, "E88.right", {"start": v(-43.93, 111.75) * mm, "end": v(-43.93, 105.75) * mm});
            skLineSegment(sketch, "E89.bottom", {"start": v(-8.08, 2.48) * mm, "end": v(4.92, 2.48) * mm});
            skLineSegment(sketch, "E89.top", {"start": v(-8.08, -3.52) * mm, "end": v(4.92, -3.52) * mm});
            skLineSegment(sketch, "E89.left", {"start": v(-8.08, 2.48) * mm, "end": v(-8.08, -3.52) * mm});
            skLineSegment(sketch, "E89.right", {"start": v(4.92, 2.48) * mm, "end": v(4.92, -3.52) * mm});
            skLineSegment(sketch, "E90.bottom", {"start": v(86.68, 3.15) * mm, "end": v(99.68, 3.15) * mm});
            skLineSegment(sketch, "E90.top", {"start": v(86.68, -2.85) * mm, "end": v(99.68, -2.85) * mm});
            skLineSegment(sketch, "E90.left", {"start": v(86.68, 3.15) * mm, "end": v(86.68, -2.85) * mm});
            skLineSegment(sketch, "E90.right", {"start": v(99.68, 3.15) * mm, "end": v(99.68, -2.85) * mm});
            skArc(sketch, "E91", {"start": v(-264.27, -184.73) * mm, "mid": v(-248.55, -174.9) * mm, "end": v(-239, -159) * mm});
            skArc(sketch, "E92", {"start": v(-175, -159) * mm, "mid": v(-190, -152.22) * mm, "end": v(-205, -159) * mm});
            skArc(sketch, "E93.MirrorCS", {"start": v(-175, 159) * mm, "mid": v(-190, 152.22) * mm, "end": v(-205, 159) * mm});
            skLineSegment(sketch, "E94.top", {"start": v(189.44, -9) * mm, "end": v(235, -9) * mm});
            skLineSegment(sketch, "E95", {"start": v(189.44, 9) * mm, "end": v(235, 9) * mm});
            skLineSegment(sketch, "E96", {"start": v(235, 9) * mm, "end": v(235, 20) * mm});
            skLineSegment(sketch, "E97", {"start": v(235, -20) * mm, "end": v(235, -9) * mm});
            skArc(sketch, "E98", {"start": v(189.44, 9) * mm, "mid": v(184.46, 0) * mm, "end": v(189.44, -9) * mm});
            skLineSegment(sketch, "E99", {"start": v(539.2, -54) * mm, "end": v(539.2, -94) * mm});
            skLineSegment(sketch, "E100.bottom", {"start": v(623.05, -26.68) * mm, "end": v(455.34, -26.68) * mm});
            skLineSegment(sketch, "E100.top", {"start": v(623.05, -118.68) * mm, "end": v(455.34, -118.68) * mm});
            skLineSegment(sketch, "E100.left", {"start": v(623.05, -26.68) * mm, "end": v(623.05, -118.68) * mm});
            skLineSegment(sketch, "E100.right", {"start": v(455.34, -26.68) * mm, "end": v(455.34, -118.68) * mm});
            skPoint(sketch, "E100.middle", {"position": v(539.2, -72.68) * mm});
            skPoint(sketch, "E101.orphan", {"position": v(539.2, -91.36) * mm});
            skLineSegment(sketch, "E102", {"start": v(455.34, -118.68) * mm, "end": v(455.34, -168.68) * mm, "construction": true});
            skLineSegment(sketch, "E103.left", {"start": v(480.71, -86.63) * mm, "end": v(467.54, -86.63) * mm});
            skPoint(sketch, "E103.middle", {"position": v(474.09, -71.63) * mm});
            skLineSegment(sketch, "E104", {"start": v(461.82, -58.48) * mm, "end": v(474.09, -71.63) * mm});
            skLineSegment(sketch, "E105", {"start": v(486.36, -58.48) * mm, "end": v(474.09, -71.63) * mm});
            skLineSegment(sketch, "E106.trimOffspring", {"start": v(488.09, -71.63) * mm, "end": v(488.09, -59.17) * mm});
            skLineSegment(sketch, "E107.trimOffspring", {"start": v(477.03, -74.78) * mm, "end": v(488.09, -86.63) * mm});
            skLineSegment(sketch, "E108.trimOffspring", {"start": v(471.15, -74.78) * mm, "end": v(460.09, -86.63) * mm});
            skPoint(sketch, "E109.orphan", {"position": v(460.09, -71.63) * mm});
            skLineSegment(sketch, "E110.trimOffspring", {"start": v(460.09, -71.63) * mm, "end": v(460.09, -59.17) * mm});
            skPoint(sketch, "E103.bottom.end.orphan", {"position": v(488.09, -74.76) * mm});
            skPoint(sketch, "E111.visualSharp", {"position": v(488.09, -56.63) * mm});
            skArc(sketch, "E111.filletArc", {"start": v(488.09, -59.17) * mm, "mid": v(487.46, -58.24) * mm, "end": v(486.36, -58.48) * mm});
            skPoint(sketch, "E112.visualSharp", {"position": v(460.09, -56.63) * mm});
            skArc(sketch, "E112.filletArc", {"start": v(461.82, -58.48) * mm, "mid": v(460.72, -58.24) * mm, "end": v(460.09, -59.17) * mm});
            skLineSegment(sketch, "E113.0", {"start": v(459.09, -71.63) * mm, "end": v(459.09, -59.17) * mm});
            skArc(sketch, "E113.1", {"start": v(462.55, -57.8) * mm, "mid": v(460.36, -57.3) * mm, "end": v(459.09, -59.17) * mm});
            skLineSegment(sketch, "E113.2", {"start": v(489.09, -71.63) * mm, "end": v(489.09, -59.17) * mm});
            skArc(sketch, "E113.3", {"start": v(489.09, -59.17) * mm, "mid": v(487.82, -57.3) * mm, "end": v(485.63, -57.8) * mm});
            skLineSegment(sketch, "E113.4", {"start": v(485.63, -57.8) * mm, "end": v(474.09, -70.16) * mm});
            skLineSegment(sketch, "E113.5", {"start": v(462.55, -57.8) * mm, "end": v(474.09, -70.16) * mm});
            skLineSegment(sketch, "E114.0", {"start": v(477.84, -74.19) * mm, "end": v(488.09, -85.16) * mm});
            skLineSegment(sketch, "E115.0", {"start": v(470.34, -74.19) * mm, "end": v(460.09, -85.16) * mm});
            skLineSegment(sketch, "E116.0", {"start": v(480.71, -85.63) * mm, "end": v(467.54, -85.63) * mm});
            skLineSegment(sketch, "E117", {"start": v(488.09, -71.63) * mm, "end": v(489.09, -71.63) * mm});
            skLineSegment(sketch, "E118", {"start": v(477.84, -74.19) * mm, "end": v(477.03, -74.78) * mm});
            skLineSegment(sketch, "E119", {"start": v(470.34, -74.19) * mm, "end": v(471.15, -74.78) * mm});
            skLineSegment(sketch, "E120", {"start": v(467.54, -85.63) * mm, "end": v(467.54, -86.63) * mm});
            skLineSegment(sketch, "E121", {"start": v(480.71, -86.63) * mm, "end": v(480.71, -85.63) * mm});
            skLineSegment(sketch, "E122", {"start": v(460.09, -71.63) * mm, "end": v(459.09, -71.63) * mm});
            skLineSegment(sketch, "E123", {"start": v(489.09, -86.24) * mm, "end": v(489.09, -80.93) * mm});
            skLineSegment(sketch, "E124", {"start": v(488.09, -85.16) * mm, "end": v(488.09, -80.93) * mm});
            skLineSegment(sketch, "E125", {"start": v(488.09, -80.93) * mm, "end": v(489.09, -80.93) * mm});
            skLineSegment(sketch, "E126", {"start": v(489.09, -86.24) * mm, "end": v(489.09, -90.76) * mm});
            skLineSegment(sketch, "E127", {"start": v(489.09, -90.76) * mm, "end": v(488.09, -90.76) * mm});
            skLineSegment(sketch, "E128", {"start": v(488.09, -90.76) * mm, "end": v(488.09, -86.63) * mm});
            skLineSegment(sketch, "E129", {"start": v(474.09, -71.63) * mm, "end": v(474.09, -83.06) * mm, "construction": true});
            skLineSegment(sketch, "E130.MirrorCS", {"start": v(460.09, -90.76) * mm, "end": v(460.09, -86.63) * mm});
            skLineSegment(sketch, "E131.MirrorCS", {"start": v(459.09, -86.24) * mm, "end": v(459.09, -80.93) * mm});
            skLineSegment(sketch, "E132.MirrorCS", {"start": v(459.09, -86.24) * mm, "end": v(459.09, -90.76) * mm});
            skLineSegment(sketch, "E133.MirrorCS", {"start": v(459.09, -90.76) * mm, "end": v(460.09, -90.76) * mm});
            skLineSegment(sketch, "E134.MirrorCS", {"start": v(460.09, -80.93) * mm, "end": v(459.09, -80.93) * mm});
            skLineSegment(sketch, "E135.MirrorCS", {"start": v(460.09, -85.16) * mm, "end": v(460.09, -80.93) * mm});
            skLineSegment(sketch, "E136.bottom", {"start": v(459.09, -56.63) * mm, "end": v(459.09, -86.63) * mm, "construction": true});
            skLineSegment(sketch, "E136.top", {"start": v(489.09, -56.63) * mm, "end": v(489.09, -86.63) * mm, "construction": true});
            skLineSegment(sketch, "E136.left", {"start": v(459.09, -56.63) * mm, "end": v(489.09, -56.63) * mm, "construction": true});
            skLineSegment(sketch, "E136.right", {"start": v(459.09, -86.63) * mm, "end": v(489.09, -86.63) * mm, "construction": true});
            skPoint(sketch, "E137.orphan", {"position": v(460.09, -86.63) * mm});
            skCircle(sketch, "E138", {"center": v(-210, -12.77) * mm, "radius": 5 * mm});
            skCircle(sketch, "E139.0.1.0", {"center": v(-210, -21.77) * mm, "radius": 5 * mm});
            skLineSegment(sketch, "E139.direction1", {"start": v(-210, -12.77) * mm, "end": v(-185, -12.77) * mm, "construction": true});
            skLineSegment(sketch, "E139.direction2", {"start": v(-210, -12.77) * mm, "end": v(-210, -21.77) * mm, "construction": true});
            skLineSegment(sketch, "E140", {"start": v(-215, -21.77) * mm, "end": v(-215, -12.77) * mm});
            skLineSegment(sketch, "E141", {"start": v(-205, -21.77) * mm, "end": v(-205, -12.77) * mm});
            skSolve(sketch);
        }
        {
            var Q0;
            Q0=makeQuery(id+"F0.imprint","IMPRINT",FACE,{"disambiguationData":[TD([[makeQuery(id+"F0.imprint","IMPRINT",EDGE,{"derivedFrom":sQuery(id+"F0.wireOp",EDGE,"E0.right")}),-1.0]])]});
            var Q1;
            {var subQ0=sQuery(id+"F0.wireOp",EDGE,"E36.MirrorCS");Q1=makeQuery(id+"F0.imprint","IMPRINT",FACE,{"disambiguationData":[TD([[makeQuery(id+"F0.imprint","IMPRINT",EDGE,{"derivedFrom":subQ0}),-1.0]])]});}
            var Q2;
            {var subQ0=sQuery(id+"F0.wireOp",EDGE,"E7");Q2=makeQuery(id+"F0.imprint","IMPRINT",FACE,{"disambiguationData":[TD([[makeQuery(id+"F0.imprint","IMPRINT",EDGE,{"derivedFrom":subQ0}),1.0]])]});}
            var Q3;
            Q3=makeQuery(id+"F0.imprint","IMPRINT",FACE,{"disambiguationData":[TD([[makeQuery(id+"F0.imprint","IMPRINT",EDGE,{"derivedFrom":sQuery(id+"F0.wireOp",EDGE,"0a756d12-7db5-462a-ba43-cb5d52a6b9f4.left")}),1.0]])]});
            var Q4;
            Q4=makeQuery(id+"F0.imprint","IMPRINT",FACE,{"disambiguationData":[TD([[makeQuery(id+"F0.imprint","IMPRINT",EDGE,{"derivedFrom":sQuery(id+"F0.wireOp",EDGE,"E75.0.1.0")}),1.0]])]});
            extrude(context, id + "F1", {"entities" : qUnion([Q0, Q1, Q2, Q3, Q4]), "depth" : 4 * mm});
        }
    });
